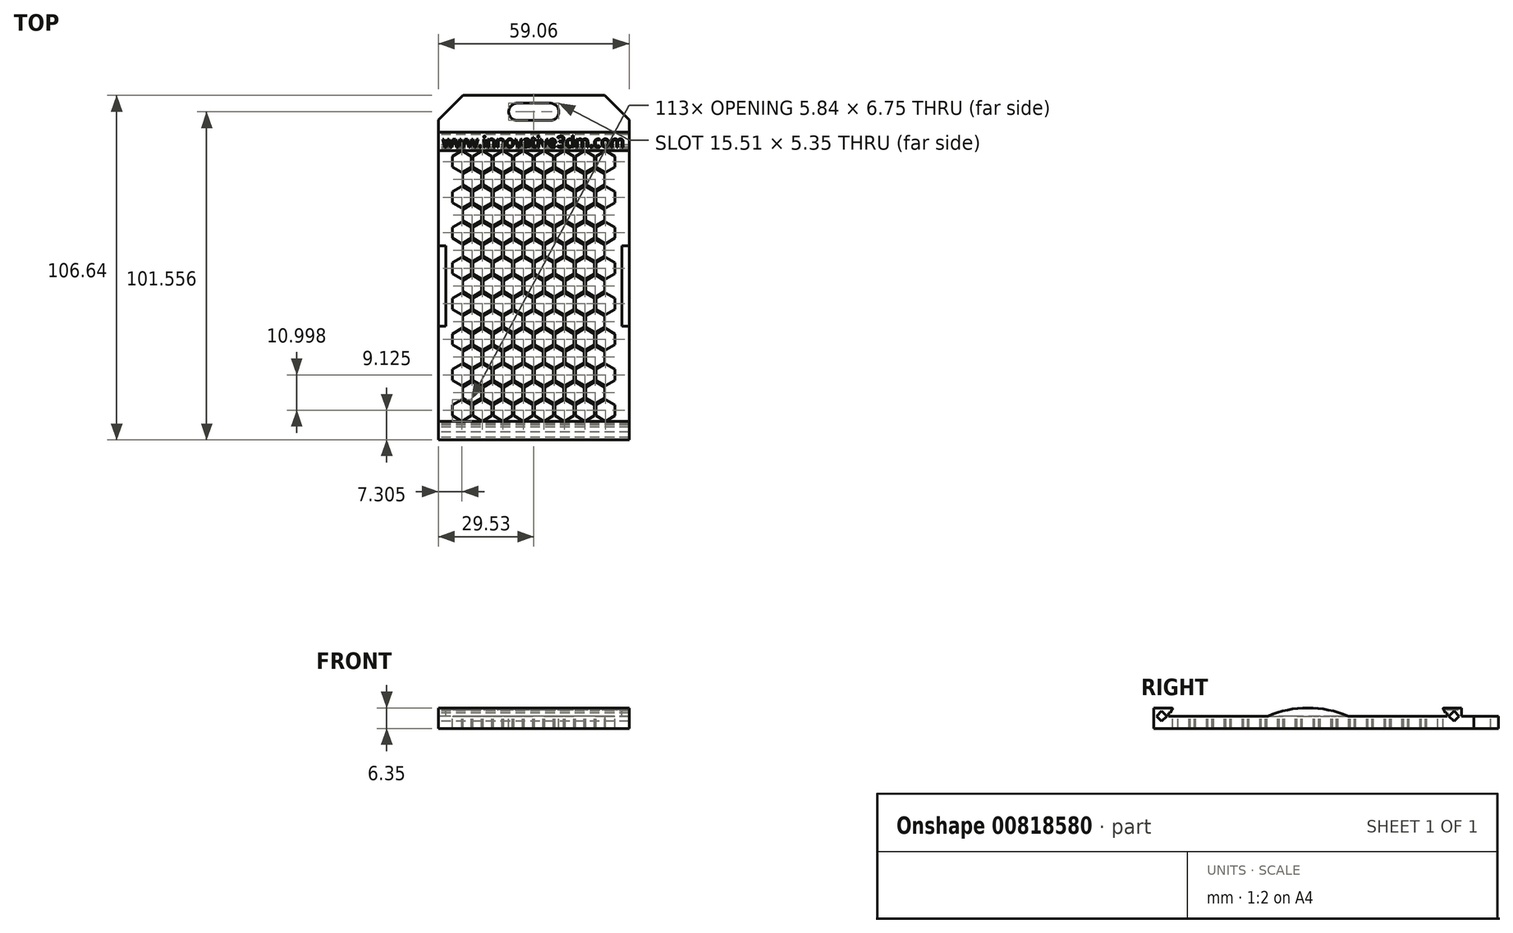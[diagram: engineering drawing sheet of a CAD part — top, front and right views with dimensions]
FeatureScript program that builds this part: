
annotation { "Feature Type Name" : "Feature", "Feature Type Description" : "" }
export const myFeature = defineFeature(function(context is Context, id is Id, definition is map)
    precondition{}
    {
        {
            var Q0;
            Q0=qCreatedBy(makeId("Right.planeOp"),FACE);
            var sketch = newSketch(context, id + "F0", { "sketchPlane" : qUnion([Q0])});
            skLineSegment(sketch, "E0.bottom", {"start": v(0, 0) * mm, "end": v(47.63, 0) * mm});
            skLineSegment(sketch, "E0.top", {"start": v(42.13, 6.35) * mm, "end": v(47.63, 6.35) * mm});
            skLineSegment(sketch, "E0.right", {"start": v(47.63, 0) * mm, "end": v(47.63, 6.35) * mm});
            skLineSegment(sketch, "E1", {"start": v(42.86, 3.81) * mm, "end": v(0, 3.81) * mm});
            skLineSegment(sketch, "E2", {"start": v(0, 0) * mm, "end": v(0, 12.7) * mm, "construction": true});
            skLineSegment(sketch, "E3.MirrorCS", {"start": v(0, 0) * mm, "end": v(-47.63, 0) * mm});
            skLineSegment(sketch, "E4.MirrorCS", {"start": v(-42.13, 6.35) * mm, "end": v(-47.63, 6.35) * mm});
            skLineSegment(sketch, "E5.MirrorCS", {"start": v(-47.63, 0) * mm, "end": v(-47.63, 6.35) * mm});
            skLineSegment(sketch, "E6.MirrorCS", {"start": v(-42.86, 3.81) * mm, "end": v(0, 3.81) * mm});
            skLineSegment(sketch, "E7", {"start": v(42.86, 3.81) * mm, "end": v(47.63, 3.81) * mm, "construction": true});
            skCircle(sketch, "E8.cCircle", {"center": v(45.24, 3.81) * mm, "radius": 1.59 * mm, "construction": true});
            skPoint(sketch, "E8.cCircle.perimeterSnap0", {"position": v(45.24, 3.81) * mm});
            skLineSegment(sketch, "E8.0", {"start": v(45.24, 2.22) * mm, "end": v(43.66, 3.8) * mm});
            skPoint(sketch, "E8.0.startSnap0", {"position": v(45.24, 3.81) * mm});
            skLineSegment(sketch, "E8.1", {"start": v(43.66, 3.81) * mm, "end": v(45.24, 5.4) * mm});
            skLineSegment(sketch, "E8.2", {"start": v(45.24, 5.4) * mm, "end": v(46.83, 3.81) * mm});
            skLineSegment(sketch, "E8.3", {"start": v(46.83, 3.81) * mm, "end": v(45.24, 2.22) * mm});
            skLineSegment(sketch, "E9.MirrorCS", {"start": v(-46.83, 3.81) * mm, "end": v(-45.24, 2.22) * mm});
            skLineSegment(sketch, "E10.MirrorCS", {"start": v(-45.24, 5.4) * mm, "end": v(-46.83, 3.81) * mm});
            skLineSegment(sketch, "E11.MirrorCS", {"start": v(-45.24, 2.22) * mm, "end": v(-43.66, 3.8) * mm});
            skLineSegment(sketch, "E12.MirrorCS", {"start": v(-43.66, 3.81) * mm, "end": v(-45.24, 5.4) * mm});
            skLineSegment(sketch, "E13.bottom", {"start": v(47.63, 3.81) * mm, "end": v(59.02, 3.81) * mm});
            skLineSegment(sketch, "E13.top", {"start": v(47.63, 0) * mm, "end": v(59.02, 0) * mm});
            skLineSegment(sketch, "E13.left", {"start": v(47.63, 3.81) * mm, "end": v(47.63, 0) * mm});
            skLineSegment(sketch, "E13.right", {"start": v(59.02, 3.81) * mm, "end": v(59.02, 0) * mm});
            skLineSegment(sketch, "E14", {"start": v(42.86, 4.83) * mm, "end": v(43.11, 4.83) * mm});
            skLineSegment(sketch, "E15", {"start": v(43.11, 4.83) * mm, "end": v(43.11, 3.81) * mm});
            skLineSegment(sketch, "E16", {"start": v(43.11, 3.81) * mm, "end": v(42.86, 3.81) * mm});
            skLineSegment(sketch, "E17", {"start": v(-42.86, 4.83) * mm, "end": v(-43.1, 4.83) * mm});
            skLineSegment(sketch, "E18", {"start": v(-43.1, 4.83) * mm, "end": v(-43.1, 3.81) * mm});
            skLineSegment(sketch, "E19", {"start": v(-43.1, 3.81) * mm, "end": v(-42.86, 3.81) * mm});
            skPoint(sketch, "E20.orphan", {"position": v(-42.06, 6.35) * mm});
            skPoint(sketch, "E21.visualSharp", {"position": v(-41.58, 6.35) * mm});
            skArc(sketch, "E21.filletArc", {"start": v(-41.93, 5.93) * mm, "mid": v(-41.9, 6.2) * mm, "end": v(-42.13, 6.35) * mm});
            skPoint(sketch, "E22.orphan", {"position": v(42.06, 6.35) * mm});
            skPoint(sketch, "E23.visualSharp", {"position": v(41.58, 6.35) * mm});
            skArc(sketch, "E23.filletArc", {"start": v(42.13, 6.35) * mm, "mid": v(41.9, 6.2) * mm, "end": v(41.93, 5.93) * mm});
            skLineSegment(sketch, "E24", {"start": v(42.86, 4.83) * mm, "end": v(42.6, 4.83) * mm});
            skLineSegment(sketch, "E25", {"start": v(42.6, 4.83) * mm, "end": v(41.93, 5.93) * mm});
            skLineSegment(sketch, "E26", {"start": v(-42.86, 4.83) * mm, "end": v(-42.6, 4.83) * mm});
            skLineSegment(sketch, "E27", {"start": v(-42.6, 4.83) * mm, "end": v(-41.93, 5.93) * mm});
            skSolve(sketch);
        }
        {
            var Q0;
            Q0 = qSketchRegion(id + "F0", true);
            extrude(context, id + "F1", {"entities" : qUnion([Q0]), "endBound" : BoundingType.SYMMETRIC, "depth" : 59.05 * mm, "offsetDistance" : 25.4 * mm});
        }
        {
            var Q0;
            Q0=makeQuery(id+"F1.opExtrude","CAP_FACE",FACE,{"disambiguationData":[OSD([sQuery(id+"F0.wireOp",EDGE,"E0.bottom"),sQuery(id+"F0.wireOp",EDGE,"E0.top"),sQuery(id+"F0.wireOp",EDGE,"E0.right"),sQuery(id+"F0.wireOp",EDGE,"gyNRLkVu-gDWa-j0yL-LBTd-Hr4iBRcMcfl1"),sQuery(id+"F0.wireOp",EDGE,"E1"),sQuery(id+"F0.wireOp",EDGE,"KyRSDgAd-UBMl-goyb-JxHU-d5xV0LulEB9J"),sQuery(id+"F0.wireOp",EDGE,"0e1NTcIS-lz3a-VeYZ-tNHN-98BEs02OGzgN"),sQuery(id+"F0.wireOp",EDGE,"e9ce5134-ec22-4a58-8b23-488e075d9638.filletArc"),sQuery(id+"F0.wireOp",EDGE,"9cae3bd2-e31c-4099-b72a-596a19319f310.MirrorCS"),sQuery(id+"F0.wireOp",EDGE,"9cae3bd2-e31c-4099-b72a-596a19319f311.MirrorCS"),sQuery(id+"F0.wireOp",EDGE,"9cae3bd2-e31c-4099-b72a-596a19319f312.MirrorCS"),sQuery(id+"F0.wireOp",EDGE,"9cae3bd2-e31c-4099-b72a-596a19319f313.MirrorCS"),sQuery(id+"F0.wireOp",EDGE,"E3.MirrorCS"),sQuery(id+"F0.wireOp",EDGE,"E4.MirrorCS"),sQuery(id+"F0.wireOp",EDGE,"E5.MirrorCS"),sQuery(id+"F0.wireOp",EDGE,"E6.MirrorCS")])],"isStart":false});
            var sketch = newSketch(context, id + "F2", { "sketchPlane" : qUnion([Q0])});
            skLineSegment(sketch, "E28", {"start": v(0, 0) * mm, "end": v(0, -25.4) * mm, "construction": true});
            skArc(sketch, "E29", {"start": v(19.05, 0) * mm, "mid": v(0, 6.35) * mm, "end": v(-19.05, 0) * mm});
            skLineSegment(sketch, "E30", {"start": v(19.05, 0) * mm, "end": v(-19.05, 0) * mm});
            skSolve(sketch);
        }
        {
            var Q0;
            {var subQ0=sQuery(id+"F2.wireOp",EDGE,"E29");var subQ1=makeQuery(id+"F1.opExtrude","CAP_EDGE",EDGE,{"disambiguationData":[OSD([sQuery(id+"F0.wireOp",EDGE,"E1"),sQuery(id+"F0.wireOp",EDGE,"E6.MirrorCS")])],"isStart":false});var subQ2=makeQuery(id+"F2.imprint","INTERSECT",VERTEX,{"disambiguationData":[OD(0.0)],"derivedFrom":[subQ1,subQ0]});Q0=makeQuery(id+"F2.imprint","IMPRINT",FACE,{"disambiguationData":[TD([[makeQuery(id+"F2.imprint","IMPRINT",EDGE,{"disambiguationData":[TD([[subQ2,-1.0]])],"derivedFrom":subQ0}),1.0]])]});}
            var Q1;
            Q1=sQuery(id+"F2.wireOp",EDGE,"E29");
            extrude(context, id + "F3", {"entities" : qUnion([Q0]), "operationType" : NewBodyOperationType.ADD, "surfaceEntities" : qUnion([Q1]), "oppositeDirection" : true, "depth" : 2.3 * mm, "offsetDistance" : 25.4 * mm});
        }
        {
            var Q0;
            Q0=makeQuery(id+"F1.opExtrude","SWEPT_BODY",BODY,{"disambiguationData":[OSD([sQuery(id+"F0.wireOp",EDGE,"E0.bottom"),sQuery(id+"F0.wireOp",EDGE,"E0.top"),sQuery(id+"F0.wireOp",EDGE,"E0.right"),sQuery(id+"F0.wireOp",EDGE,"gyNRLkVu-gDWa-j0yL-LBTd-Hr4iBRcMcfl1"),sQuery(id+"F0.wireOp",EDGE,"E1"),sQuery(id+"F0.wireOp",EDGE,"KyRSDgAd-UBMl-goyb-JxHU-d5xV0LulEB9J"),sQuery(id+"F0.wireOp",EDGE,"0e1NTcIS-lz3a-VeYZ-tNHN-98BEs02OGzgN"),sQuery(id+"F0.wireOp",EDGE,"e9ce5134-ec22-4a58-8b23-488e075d9638.filletArc"),sQuery(id+"F0.wireOp",EDGE,"9cae3bd2-e31c-4099-b72a-596a19319f310.MirrorCS"),sQuery(id+"F0.wireOp",EDGE,"9cae3bd2-e31c-4099-b72a-596a19319f311.MirrorCS"),sQuery(id+"F0.wireOp",EDGE,"9cae3bd2-e31c-4099-b72a-596a19319f312.MirrorCS"),sQuery(id+"F0.wireOp",EDGE,"9cae3bd2-e31c-4099-b72a-596a19319f313.MirrorCS"),sQuery(id+"F0.wireOp",EDGE,"E3.MirrorCS"),sQuery(id+"F0.wireOp",EDGE,"E4.MirrorCS"),sQuery(id+"F0.wireOp",EDGE,"E5.MirrorCS"),sQuery(id+"F0.wireOp",EDGE,"E6.MirrorCS")])]});
            var Q1;
            Q1=qCreatedBy(makeId("Right.planeOp"),FACE);
            mirror(context, id + "F4", {"operationType" : NewBodyOperationType.ADD, "entities" : qUnion([Q0]), "mirrorPlane" : qUnion([Q1])});
        }
        {
            var Q0;
            Q0=makeQuery(id+"F1.opExtrude","SWEPT_FACE",FACE,{"disambiguationData":[OSD([sQuery(id+"F0.wireOp",EDGE,"E1"),sQuery(id+"F0.wireOp",EDGE,"E6.MirrorCS")])]});
            var sketch = newSketch(context, id + "F5", { "sketchPlane" : qUnion([Q0])});
            skCircle(sketch, "E31.cCircle", {"center": v(0, 0) * mm, "radius": 2.92 * mm, "construction": true});
            skLineSegment(sketch, "E31.0", {"start": v(2.92, 1.69) * mm, "end": v(2.92, -1.69) * mm});
            skLineSegment(sketch, "E31.1", {"start": v(2.92, -1.69) * mm, "end": v(0, -3.37) * mm});
            skLineSegment(sketch, "E31.2", {"start": v(0, -3.37) * mm, "end": v(-2.92, -1.69) * mm});
            skLineSegment(sketch, "E31.3", {"start": v(-2.92, -1.69) * mm, "end": v(-2.92, 1.69) * mm});
            skLineSegment(sketch, "E31.4", {"start": v(-2.92, 1.69) * mm, "end": v(0, 3.37) * mm});
            skLineSegment(sketch, "E31.5", {"start": v(0, 3.37) * mm, "end": v(2.92, 1.69) * mm});
            skPoint(sketch, "E31.0.midPoint", {"position": v(2.92, 0) * mm});
            skLineSegment(sketch, "E32.1.0.0", {"start": v(6.35, 3.37) * mm, "end": v(9.27, 1.69) * mm});
            skLineSegment(sketch, "E32.1.0.1", {"start": v(3.43, 1.69) * mm, "end": v(6.35, 3.37) * mm});
            skLineSegment(sketch, "E32.1.0.2", {"start": v(3.43, -1.69) * mm, "end": v(3.43, 1.69) * mm});
            skLineSegment(sketch, "E32.1.0.3", {"start": v(6.35, -3.37) * mm, "end": v(3.43, -1.69) * mm});
            skLineSegment(sketch, "E32.1.0.4", {"start": v(9.27, -1.69) * mm, "end": v(6.35, -3.37) * mm});
            skLineSegment(sketch, "E32.1.0.5", {"start": v(9.27, 1.69) * mm, "end": v(9.27, -1.69) * mm});
            skLineSegment(sketch, "E32.2.0.0", {"start": v(12.7, 3.37) * mm, "end": v(15.62, 1.69) * mm});
            skLineSegment(sketch, "E32.2.0.1", {"start": v(9.78, 1.69) * mm, "end": v(12.7, 3.37) * mm});
            skLineSegment(sketch, "E32.2.0.2", {"start": v(9.78, -1.69) * mm, "end": v(9.78, 1.69) * mm});
            skLineSegment(sketch, "E32.2.0.3", {"start": v(12.7, -3.37) * mm, "end": v(9.78, -1.69) * mm});
            skLineSegment(sketch, "E32.2.0.4", {"start": v(15.62, -1.69) * mm, "end": v(12.7, -3.37) * mm});
            skLineSegment(sketch, "E32.2.0.5", {"start": v(15.62, 1.69) * mm, "end": v(15.62, -1.69) * mm});
            skLineSegment(sketch, "E32.direction1", {"start": v(-2.92, -1.69) * mm, "end": v(3.43, -1.69) * mm, "construction": true});
            skLineSegment(sketch, "E33.0.3.0", {"start": v(19.05, 3.37) * mm, "end": v(21.97, 1.69) * mm});
            skLineSegment(sketch, "E33.3.3.0", {"start": v(16.13, 1.69) * mm, "end": v(19.05, 3.37) * mm});
            skLineSegment(sketch, "E33.6.3.0", {"start": v(16.13, -1.69) * mm, "end": v(16.13, 1.69) * mm});
            skLineSegment(sketch, "E33.9.3.0", {"start": v(19.05, -3.37) * mm, "end": v(16.13, -1.69) * mm});
            skLineSegment(sketch, "E33.12.3.0", {"start": v(21.97, -1.69) * mm, "end": v(19.05, -3.37) * mm});
            skLineSegment(sketch, "E33.15.3.0", {"start": v(21.97, 1.69) * mm, "end": v(21.97, -1.69) * mm});
            skLineSegment(sketch, "E34", {"start": v(2.92, 1.69) * mm, "end": v(3.43, 1.69) * mm, "construction": true});
            skLineSegment(sketch, "E35", {"start": v(3.18, 1.69) * mm, "end": v(3.18, 5.5) * mm, "construction": true});
            skLineSegment(sketch, "E36.0", {"start": v(0.25, 3.81) * mm, "end": v(3.17, 2.13) * mm, "construction": true});
            skLineSegment(sketch, "E37", {"start": v(0, 0) * mm, "end": v(1.46, 2.53) * mm, "construction": true});
            skLineSegment(sketch, "E38", {"start": v(1.46, 2.53) * mm, "end": v(3.18, 5.5) * mm, "construction": true});
            skCircle(sketch, "E39.cCircle", {"center": v(3.18, 5.5) * mm, "radius": 2.92 * mm, "construction": true});
            skPoint(sketch, "E39.cCircle.perimeterSnap0", {"position": v(1.71, 2.97) * mm});
            skLineSegment(sketch, "E39.0", {"start": v(3.18, 2.13) * mm, "end": v(0.25, 3.81) * mm});
            skLineSegment(sketch, "E39.1", {"start": v(0.25, 3.81) * mm, "end": v(0.25, 7.19) * mm});
            skLineSegment(sketch, "E39.2", {"start": v(0.25, 7.19) * mm, "end": v(3.18, 8.87) * mm});
            skLineSegment(sketch, "E39.3", {"start": v(3.18, 8.87) * mm, "end": v(6.1, 7.19) * mm});
            skLineSegment(sketch, "E39.4", {"start": v(6.1, 7.19) * mm, "end": v(6.1, 3.81) * mm});
            skLineSegment(sketch, "E39.5", {"start": v(6.1, 3.81) * mm, "end": v(3.18, 2.13) * mm});
            skPoint(sketch, "E39.0.midPoint", {"position": v(1.71, 2.97) * mm});
            skPoint(sketch, "E39.0.midPoint.positionSnap0", {"position": v(1.71, 2.97) * mm});
            skLineSegment(sketch, "E40.1.0.0", {"start": v(6.6, 7.19) * mm, "end": v(9.53, 8.87) * mm});
            skLineSegment(sketch, "E40.1.0.1", {"start": v(9.52, 8.87) * mm, "end": v(12.45, 7.19) * mm});
            skLineSegment(sketch, "E40.1.0.2", {"start": v(12.45, 7.19) * mm, "end": v(12.45, 3.81) * mm});
            skLineSegment(sketch, "E40.1.0.3", {"start": v(12.45, 3.81) * mm, "end": v(9.52, 2.13) * mm});
            skLineSegment(sketch, "E40.1.0.4", {"start": v(9.52, 2.13) * mm, "end": v(6.6, 3.81) * mm});
            skLineSegment(sketch, "E40.1.0.5", {"start": v(6.6, 3.81) * mm, "end": v(6.6, 7.19) * mm});
            skLineSegment(sketch, "E40.2.0.0", {"start": v(12.95, 7.19) * mm, "end": v(15.88, 8.87) * mm});
            skLineSegment(sketch, "E40.2.0.1", {"start": v(15.87, 8.87) * mm, "end": v(18.8, 7.19) * mm});
            skLineSegment(sketch, "E40.2.0.2", {"start": v(18.8, 7.19) * mm, "end": v(18.8, 3.81) * mm});
            skLineSegment(sketch, "E40.2.0.3", {"start": v(18.8, 3.81) * mm, "end": v(15.87, 2.13) * mm});
            skLineSegment(sketch, "E40.2.0.4", {"start": v(15.88, 2.13) * mm, "end": v(12.95, 3.81) * mm});
            skLineSegment(sketch, "E40.2.0.5", {"start": v(12.95, 3.81) * mm, "end": v(12.95, 7.19) * mm});
            skLineSegment(sketch, "E40.direction1", {"start": v(0.25, 3.81) * mm, "end": v(6.6, 3.81) * mm, "construction": true});
            skLineSegment(sketch, "E41.0.3.0", {"start": v(19.3, 7.19) * mm, "end": v(22.23, 8.87) * mm});
            skLineSegment(sketch, "E41.3.3.0", {"start": v(22.23, 8.87) * mm, "end": v(25.15, 7.19) * mm});
            skLineSegment(sketch, "E41.6.3.0", {"start": v(25.15, 7.19) * mm, "end": v(25.15, 3.81) * mm});
            skLineSegment(sketch, "E41.9.3.0", {"start": v(25.15, 3.81) * mm, "end": v(22.23, 2.13) * mm});
            skLineSegment(sketch, "E41.12.3.0", {"start": v(22.23, 2.13) * mm, "end": v(19.3, 3.81) * mm});
            skLineSegment(sketch, "E41.15.3.0", {"start": v(19.3, 3.81) * mm, "end": v(19.3, 7.19) * mm});
            skLineSegment(sketch, "E42.1.0.0", {"start": v(-9.27, -1.69) * mm, "end": v(-9.27, 1.69) * mm});
            skLineSegment(sketch, "E42.1.0.1", {"start": v(-9.27, 1.69) * mm, "end": v(-6.35, 3.37) * mm});
            skLineSegment(sketch, "E42.1.0.2", {"start": v(-6.35, 3.37) * mm, "end": v(-3.43, 1.69) * mm});
            skLineSegment(sketch, "E42.1.0.3", {"start": v(-3.43, 1.69) * mm, "end": v(-3.43, -1.69) * mm});
            skLineSegment(sketch, "E42.1.0.4", {"start": v(-3.43, -1.69) * mm, "end": v(-6.35, -3.37) * mm});
            skLineSegment(sketch, "E42.1.0.5", {"start": v(-6.35, -3.37) * mm, "end": v(-9.27, -1.69) * mm});
            skLineSegment(sketch, "E42.2.0.0", {"start": v(-15.62, -1.69) * mm, "end": v(-15.62, 1.69) * mm});
            skLineSegment(sketch, "E42.2.0.1", {"start": v(-15.62, 1.69) * mm, "end": v(-12.7, 3.37) * mm});
            skLineSegment(sketch, "E42.2.0.2", {"start": v(-12.7, 3.37) * mm, "end": v(-9.78, 1.69) * mm});
            skLineSegment(sketch, "E42.2.0.3", {"start": v(-9.78, 1.69) * mm, "end": v(-9.78, -1.69) * mm});
            skLineSegment(sketch, "E42.2.0.4", {"start": v(-9.78, -1.69) * mm, "end": v(-12.7, -3.37) * mm});
            skLineSegment(sketch, "E42.2.0.5", {"start": v(-12.7, -3.37) * mm, "end": v(-15.62, -1.69) * mm});
            skLineSegment(sketch, "E42.direction1", {"start": v(-2.92, -1.69) * mm, "end": v(-9.27, -1.69) * mm, "construction": true});
            skLineSegment(sketch, "E43.0.3.0", {"start": v(-21.97, -1.69) * mm, "end": v(-21.97, 1.69) * mm});
            skLineSegment(sketch, "E43.3.3.0", {"start": v(-21.97, 1.69) * mm, "end": v(-19.05, 3.37) * mm});
            skLineSegment(sketch, "E43.6.3.0", {"start": v(-19.05, 3.37) * mm, "end": v(-16.13, 1.69) * mm});
            skLineSegment(sketch, "E43.9.3.0", {"start": v(-16.13, 1.69) * mm, "end": v(-16.13, -1.69) * mm});
            skLineSegment(sketch, "E43.12.3.0", {"start": v(-16.13, -1.69) * mm, "end": v(-19.05, -3.37) * mm});
            skLineSegment(sketch, "E43.15.3.0", {"start": v(-19.05, -3.37) * mm, "end": v(-21.97, -1.69) * mm});
            skLineSegment(sketch, "E44.1.0.0", {"start": v(-6.1, 3.81) * mm, "end": v(-6.1, 7.19) * mm});
            skLineSegment(sketch, "E44.1.0.1", {"start": v(-6.1, 7.19) * mm, "end": v(-3.17, 8.87) * mm});
            skLineSegment(sketch, "E44.1.0.2", {"start": v(-3.17, 8.87) * mm, "end": v(-0.25, 7.19) * mm});
            skLineSegment(sketch, "E44.1.0.3", {"start": v(-0.25, 3.81) * mm, "end": v(-3.18, 2.13) * mm});
            skLineSegment(sketch, "E44.1.0.4", {"start": v(-0.25, 7.19) * mm, "end": v(-0.25, 3.81) * mm});
            skLineSegment(sketch, "E44.1.0.5", {"start": v(-3.17, 2.13) * mm, "end": v(-6.1, 3.81) * mm});
            skLineSegment(sketch, "E44.2.0.0", {"start": v(-12.45, 3.81) * mm, "end": v(-12.45, 7.19) * mm});
            skLineSegment(sketch, "E44.2.0.1", {"start": v(-12.45, 7.19) * mm, "end": v(-9.52, 8.87) * mm});
            skLineSegment(sketch, "E44.2.0.2", {"start": v(-9.52, 8.87) * mm, "end": v(-6.6, 7.19) * mm});
            skLineSegment(sketch, "E44.2.0.3", {"start": v(-6.6, 3.81) * mm, "end": v(-9.52, 2.13) * mm});
            skLineSegment(sketch, "E44.2.0.4", {"start": v(-6.6, 7.19) * mm, "end": v(-6.6, 3.81) * mm});
            skLineSegment(sketch, "E44.2.0.5", {"start": v(-9.52, 2.13) * mm, "end": v(-12.45, 3.81) * mm});
            skLineSegment(sketch, "E44.3.0.0", {"start": v(-18.8, 3.81) * mm, "end": v(-18.8, 7.19) * mm});
            skLineSegment(sketch, "E44.3.0.1", {"start": v(-18.8, 7.19) * mm, "end": v(-15.88, 8.87) * mm});
            skLineSegment(sketch, "E44.3.0.2", {"start": v(-15.87, 8.87) * mm, "end": v(-12.95, 7.19) * mm});
            skLineSegment(sketch, "E44.3.0.3", {"start": v(-12.95, 3.81) * mm, "end": v(-15.88, 2.13) * mm});
            skLineSegment(sketch, "E44.3.0.4", {"start": v(-12.95, 7.19) * mm, "end": v(-12.95, 3.81) * mm});
            skLineSegment(sketch, "E44.3.0.5", {"start": v(-15.88, 2.13) * mm, "end": v(-18.8, 3.81) * mm});
            skLineSegment(sketch, "E44.4.0.0", {"start": v(-25.15, 3.81) * mm, "end": v(-25.15, 7.19) * mm});
            skLineSegment(sketch, "E44.4.0.1", {"start": v(-25.15, 7.19) * mm, "end": v(-22.23, 8.87) * mm});
            skLineSegment(sketch, "E44.4.0.2", {"start": v(-22.22, 8.87) * mm, "end": v(-19.3, 7.19) * mm});
            skLineSegment(sketch, "E44.4.0.3", {"start": v(-19.3, 3.81) * mm, "end": v(-22.23, 2.13) * mm});
            skLineSegment(sketch, "E44.4.0.4", {"start": v(-19.3, 7.19) * mm, "end": v(-19.3, 3.81) * mm});
            skLineSegment(sketch, "E44.4.0.5", {"start": v(-22.23, 2.13) * mm, "end": v(-25.15, 3.81) * mm});
            skLineSegment(sketch, "E44.direction1", {"start": v(0.25, 3.81) * mm, "end": v(-6.1, 3.81) * mm, "construction": true});
            skLineSegment(sketch, "E45.0.1.0", {"start": v(-9.78, 12.68) * mm, "end": v(-9.78, 9.31) * mm});
            skLineSegment(sketch, "E45.0.1.1", {"start": v(-12.45, 14.81) * mm, "end": v(-12.45, 18.18) * mm});
            skLineSegment(sketch, "E45.0.1.2", {"start": v(-21.97, 12.68) * mm, "end": v(-19.05, 14.37) * mm});
            skLineSegment(sketch, "E45.0.1.3", {"start": v(19.05, 7.63) * mm, "end": v(16.13, 9.31) * mm});
            skLineSegment(sketch, "E45.0.1.4", {"start": v(9.27, 12.68) * mm, "end": v(9.27, 9.31) * mm});
            skLineSegment(sketch, "E45.0.1.5", {"start": v(12.7, 7.63) * mm, "end": v(9.78, 9.31) * mm});
            skLineSegment(sketch, "E45.0.1.6", {"start": v(6.6, 18.18) * mm, "end": v(9.53, 19.87) * mm});
            skLineSegment(sketch, "E45.0.1.7", {"start": v(-9.27, 9.31) * mm, "end": v(-9.27, 12.68) * mm});
            skLineSegment(sketch, "E45.0.1.8", {"start": v(-6.6, 14.81) * mm, "end": v(-9.52, 13.12) * mm});
            skLineSegment(sketch, "E45.0.1.9", {"start": v(1.46, 13.53) * mm, "end": v(3.18, 16.5) * mm, "construction": true});
            skLineSegment(sketch, "E45.0.1.10", {"start": v(-6.35, 7.63) * mm, "end": v(-9.27, 9.31) * mm});
            skLineSegment(sketch, "E45.0.1.11", {"start": v(-16.13, 12.68) * mm, "end": v(-16.13, 9.31) * mm});
            skLineSegment(sketch, "E45.0.1.12", {"start": v(-18.8, 18.18) * mm, "end": v(-15.88, 19.87) * mm});
            skLineSegment(sketch, "E45.0.1.13", {"start": v(-12.95, 18.18) * mm, "end": v(-12.95, 14.81) * mm});
            skLineSegment(sketch, "E45.0.1.14", {"start": v(22.23, 19.87) * mm, "end": v(25.15, 18.18) * mm});
            skLineSegment(sketch, "E45.0.1.15", {"start": v(6.6, 14.81) * mm, "end": v(6.6, 18.18) * mm});
            skLineSegment(sketch, "E45.0.1.16", {"start": v(21.97, 12.68) * mm, "end": v(21.97, 9.31) * mm});
            skLineSegment(sketch, "E45.0.1.17", {"start": v(12.45, 14.81) * mm, "end": v(9.52, 13.12) * mm});
            skLineSegment(sketch, "E45.0.1.18", {"start": v(-19.05, 14.37) * mm, "end": v(-16.13, 12.68) * mm});
            skLineSegment(sketch, "E45.0.1.19", {"start": v(-18.8, 14.81) * mm, "end": v(-18.8, 18.18) * mm});
            skLineSegment(sketch, "E45.0.1.20", {"start": v(9.27, 9.31) * mm, "end": v(6.35, 7.63) * mm});
            skLineSegment(sketch, "E45.0.1.21", {"start": v(6.35, 7.63) * mm, "end": v(3.43, 9.31) * mm});
            skLineSegment(sketch, "E45.0.1.22", {"start": v(3.43, 9.31) * mm, "end": v(3.43, 12.68) * mm});
            skLineSegment(sketch, "E45.0.1.23", {"start": v(3.43, 12.68) * mm, "end": v(6.35, 14.37) * mm});
            skLineSegment(sketch, "E45.0.1.24", {"start": v(6.35, 14.37) * mm, "end": v(9.27, 12.68) * mm});
            skLineSegment(sketch, "E45.0.1.25", {"start": v(0, 14.37) * mm, "end": v(2.92, 12.68) * mm});
            skLineSegment(sketch, "E45.0.1.26", {"start": v(-0.25, 14.81) * mm, "end": v(-3.17, 13.12) * mm});
            skLineSegment(sketch, "E45.0.1.27", {"start": v(-6.6, 18.18) * mm, "end": v(-6.6, 14.81) * mm});
            skLineSegment(sketch, "E45.0.1.28", {"start": v(-25.15, 18.18) * mm, "end": v(-22.23, 19.87) * mm});
            skLineSegment(sketch, "E45.0.1.29", {"start": v(-2.92, 12.68) * mm, "end": v(0, 14.37) * mm});
            skCircle(sketch, "E45.0.1.30", {"center": v(3.18, 16.5) * mm, "radius": 2.92 * mm, "construction": true});
            skLineSegment(sketch, "E45.0.1.31", {"start": v(18.8, 14.81) * mm, "end": v(15.87, 13.12) * mm});
            skLineSegment(sketch, "E45.0.1.32", {"start": v(25.15, 14.81) * mm, "end": v(22.23, 13.12) * mm});
            skLineSegment(sketch, "E45.0.1.33", {"start": v(-21.97, 9.31) * mm, "end": v(-21.97, 12.68) * mm});
            skLineSegment(sketch, "E45.0.1.34", {"start": v(0, 7.63) * mm, "end": v(-2.92, 9.31) * mm});
            skLineSegment(sketch, "E45.0.1.35", {"start": v(2.92, 9.31) * mm, "end": v(0, 7.63) * mm});
            skLineSegment(sketch, "E45.0.1.36", {"start": v(2.92, 12.68) * mm, "end": v(2.92, 9.31) * mm});
            skCircle(sketch, "E45.0.1.37", {"center": v(0, 11) * mm, "radius": 2.92 * mm, "construction": true});
            skLineSegment(sketch, "E45.0.1.38", {"start": v(9.78, 9.31) * mm, "end": v(9.78, 12.68) * mm});
            skLineSegment(sketch, "E45.0.1.39", {"start": v(9.78, 12.68) * mm, "end": v(12.7, 14.37) * mm});
            skLineSegment(sketch, "E45.0.1.40", {"start": v(12.7, 14.37) * mm, "end": v(15.62, 12.68) * mm});
            skLineSegment(sketch, "E45.0.1.41", {"start": v(21.97, 9.31) * mm, "end": v(19.05, 7.63) * mm});
            skLineSegment(sketch, "E45.0.1.42", {"start": v(12.45, 18.18) * mm, "end": v(12.45, 14.81) * mm});
            skLineSegment(sketch, "E45.0.1.43", {"start": v(-3.17, 19.87) * mm, "end": v(-0.25, 18.18) * mm});
            skLineSegment(sketch, "E45.0.1.44", {"start": v(6.1, 14.81) * mm, "end": v(3.18, 13.12) * mm});
            skLineSegment(sketch, "E45.0.1.45", {"start": v(16.13, 12.68) * mm, "end": v(19.05, 14.37) * mm});
            skLineSegment(sketch, "E45.0.1.46", {"start": v(18.8, 18.18) * mm, "end": v(18.8, 14.81) * mm});
            skLineSegment(sketch, "E45.0.1.47", {"start": v(25.15, 18.18) * mm, "end": v(25.15, 14.81) * mm});
            skLineSegment(sketch, "E45.0.1.48", {"start": v(-2.92, 9.31) * mm, "end": v(-9.27, 9.31) * mm, "construction": true});
            skLineSegment(sketch, "E45.0.1.49", {"start": v(-3.17, 13.12) * mm, "end": v(-6.1, 14.81) * mm});
            skLineSegment(sketch, "E45.0.1.50", {"start": v(-3.43, 12.68) * mm, "end": v(-3.43, 9.31) * mm});
            skLineSegment(sketch, "E45.0.1.51", {"start": v(-6.1, 14.81) * mm, "end": v(-6.1, 18.18) * mm});
            skLineSegment(sketch, "E45.0.1.52", {"start": v(0.25, 14.81) * mm, "end": v(3.17, 13.12) * mm, "construction": true});
            skLineSegment(sketch, "E45.0.1.53", {"start": v(15.62, 9.31) * mm, "end": v(12.7, 7.63) * mm});
            skLineSegment(sketch, "E45.0.1.54", {"start": v(12.95, 14.81) * mm, "end": v(12.95, 18.18) * mm});
            skLineSegment(sketch, "E45.0.1.55", {"start": v(22.23, 13.12) * mm, "end": v(19.3, 14.81) * mm});
            skLineSegment(sketch, "E45.0.1.56", {"start": v(-15.88, 13.12) * mm, "end": v(-18.8, 14.81) * mm});
            skLineSegment(sketch, "E45.0.1.57", {"start": v(19.05, 14.37) * mm, "end": v(21.97, 12.68) * mm});
            skLineSegment(sketch, "E45.0.1.58", {"start": v(6.1, 18.18) * mm, "end": v(6.1, 14.81) * mm});
            skLineSegment(sketch, "E45.0.1.59", {"start": v(0, 11) * mm, "end": v(1.46, 13.53) * mm, "construction": true});
            skLineSegment(sketch, "E45.0.1.60", {"start": v(15.87, 19.87) * mm, "end": v(18.8, 18.18) * mm});
            skLineSegment(sketch, "E45.0.1.61", {"start": v(-9.52, 13.12) * mm, "end": v(-12.45, 14.81) * mm});
            skLineSegment(sketch, "E45.0.1.62", {"start": v(9.52, 19.87) * mm, "end": v(12.45, 18.18) * mm});
            skLineSegment(sketch, "E45.0.1.63", {"start": v(-6.35, 14.37) * mm, "end": v(-3.43, 12.68) * mm});
            skLineSegment(sketch, "E45.0.1.64", {"start": v(-12.95, 14.81) * mm, "end": v(-15.88, 13.12) * mm});
            skLineSegment(sketch, "E45.0.1.65", {"start": v(3.18, 12.68) * mm, "end": v(3.18, 16.5) * mm, "construction": true});
            skLineSegment(sketch, "E45.0.1.66", {"start": v(-15.62, 12.68) * mm, "end": v(-12.7, 14.37) * mm});
            skPoint(sketch, "E45.0.1.67", {"position": v(2.92, 11) * mm});
            skLineSegment(sketch, "E45.0.1.68", {"start": v(-9.78, 9.31) * mm, "end": v(-12.7, 7.63) * mm});
            skLineSegment(sketch, "E45.0.1.69", {"start": v(-0.25, 18.18) * mm, "end": v(-0.25, 14.81) * mm});
            skLineSegment(sketch, "E45.0.1.70", {"start": v(-15.87, 19.87) * mm, "end": v(-12.95, 18.18) * mm});
            skLineSegment(sketch, "E45.0.1.71", {"start": v(15.62, 12.68) * mm, "end": v(15.62, 9.31) * mm});
            skLineSegment(sketch, "E45.0.1.72", {"start": v(-22.22, 19.87) * mm, "end": v(-19.3, 18.18) * mm});
            skLineSegment(sketch, "E45.0.1.73", {"start": v(-19.3, 18.18) * mm, "end": v(-19.3, 14.81) * mm});
            skLineSegment(sketch, "E45.0.1.74", {"start": v(19.3, 14.81) * mm, "end": v(19.3, 18.18) * mm});
            skLineSegment(sketch, "E45.0.1.75", {"start": v(-19.3, 14.81) * mm, "end": v(-22.23, 13.12) * mm});
            skLineSegment(sketch, "E45.0.1.76", {"start": v(0.25, 14.81) * mm, "end": v(0.25, 18.18) * mm});
            skLineSegment(sketch, "E45.0.1.77", {"start": v(-12.7, 14.37) * mm, "end": v(-9.78, 12.68) * mm});
            skLineSegment(sketch, "E45.0.1.78", {"start": v(15.88, 13.12) * mm, "end": v(12.95, 14.81) * mm});
            skLineSegment(sketch, "E45.0.1.79", {"start": v(16.13, 9.31) * mm, "end": v(16.13, 12.68) * mm});
            skLineSegment(sketch, "E45.0.1.80", {"start": v(-15.62, 9.31) * mm, "end": v(-15.62, 12.68) * mm});
            skLineSegment(sketch, "E45.0.1.81", {"start": v(-2.92, 9.31) * mm, "end": v(-2.92, 12.68) * mm});
            skLineSegment(sketch, "E45.0.1.82", {"start": v(12.95, 18.18) * mm, "end": v(15.88, 19.87) * mm});
            skPoint(sketch, "E45.0.1.83", {"position": v(1.71, 13.97) * mm});
            skLineSegment(sketch, "E45.0.1.84", {"start": v(-9.52, 19.87) * mm, "end": v(-6.6, 18.18) * mm});
            skLineSegment(sketch, "E45.0.1.85", {"start": v(-6.1, 18.18) * mm, "end": v(-3.17, 19.87) * mm});
            skLineSegment(sketch, "E45.0.1.86", {"start": v(0.25, 14.81) * mm, "end": v(-6.1, 14.81) * mm, "construction": true});
            skLineSegment(sketch, "E45.0.1.87", {"start": v(-3.43, 9.31) * mm, "end": v(-6.35, 7.63) * mm});
            skLineSegment(sketch, "E45.0.1.88", {"start": v(-22.23, 13.12) * mm, "end": v(-25.15, 14.81) * mm});
            skLineSegment(sketch, "E45.0.1.89", {"start": v(-12.45, 18.18) * mm, "end": v(-9.52, 19.87) * mm});
            skLineSegment(sketch, "E45.0.1.90", {"start": v(-2.92, 9.31) * mm, "end": v(3.43, 9.31) * mm, "construction": true});
            skLineSegment(sketch, "E45.0.1.91", {"start": v(3.18, 19.87) * mm, "end": v(6.1, 18.18) * mm});
            skLineSegment(sketch, "E45.0.1.92", {"start": v(19.3, 18.18) * mm, "end": v(22.23, 19.87) * mm});
            skLineSegment(sketch, "E45.0.1.93", {"start": v(-9.27, 12.68) * mm, "end": v(-6.35, 14.37) * mm});
            skLineSegment(sketch, "E45.0.1.94", {"start": v(9.52, 13.12) * mm, "end": v(6.6, 14.81) * mm});
            skLineSegment(sketch, "E45.0.1.95", {"start": v(0.25, 18.18) * mm, "end": v(3.18, 19.87) * mm});
            skLineSegment(sketch, "E45.0.1.96", {"start": v(0.25, 14.81) * mm, "end": v(6.6, 14.81) * mm, "construction": true});
            skLineSegment(sketch, "E45.0.1.97", {"start": v(3.18, 13.12) * mm, "end": v(0.25, 14.81) * mm});
            skPoint(sketch, "E45.0.1.98", {"position": v(1.71, 13.97) * mm});
            skPoint(sketch, "E45.0.1.99", {"position": v(1.71, 13.97) * mm});
            skLineSegment(sketch, "E45.0.1.100", {"start": v(2.92, 12.68) * mm, "end": v(3.43, 12.68) * mm, "construction": true});
            skLineSegment(sketch, "E45.0.1.101", {"start": v(-25.15, 14.81) * mm, "end": v(-25.15, 18.18) * mm});
            skLineSegment(sketch, "E45.0.1.102", {"start": v(-19.05, 7.63) * mm, "end": v(-21.97, 9.31) * mm});
            skLineSegment(sketch, "E45.0.1.103", {"start": v(-16.13, 9.31) * mm, "end": v(-19.05, 7.63) * mm});
            skLineSegment(sketch, "E45.0.1.104", {"start": v(-12.7, 7.63) * mm, "end": v(-15.62, 9.31) * mm});
            skLineSegment(sketch, "E45.0.2.0", {"start": v(-9.78, 23.68) * mm, "end": v(-9.78, 20.31) * mm});
            skLineSegment(sketch, "E45.0.2.1", {"start": v(-12.45, 25.8) * mm, "end": v(-12.45, 29.18) * mm});
            skLineSegment(sketch, "E45.0.2.2", {"start": v(-21.97, 23.68) * mm, "end": v(-19.05, 25.37) * mm});
            skLineSegment(sketch, "E45.0.2.3", {"start": v(19.05, 18.62) * mm, "end": v(16.13, 20.31) * mm});
            skLineSegment(sketch, "E45.0.2.4", {"start": v(9.27, 23.68) * mm, "end": v(9.27, 20.31) * mm});
            skLineSegment(sketch, "E45.0.2.5", {"start": v(12.7, 18.62) * mm, "end": v(9.78, 20.31) * mm});
            skLineSegment(sketch, "E45.0.2.6", {"start": v(6.6, 29.18) * mm, "end": v(9.53, 30.87) * mm});
            skLineSegment(sketch, "E45.0.2.7", {"start": v(-9.27, 20.31) * mm, "end": v(-9.27, 23.68) * mm});
            skLineSegment(sketch, "E45.0.2.8", {"start": v(-6.6, 25.8) * mm, "end": v(-9.52, 24.12) * mm});
            skLineSegment(sketch, "E45.0.2.9", {"start": v(1.46, 24.53) * mm, "end": v(3.18, 27.5) * mm, "construction": true});
            skLineSegment(sketch, "E45.0.2.10", {"start": v(-6.35, 18.62) * mm, "end": v(-9.27, 20.31) * mm});
            skLineSegment(sketch, "E45.0.2.11", {"start": v(-16.13, 23.68) * mm, "end": v(-16.13, 20.31) * mm});
            skLineSegment(sketch, "E45.0.2.12", {"start": v(-18.8, 29.18) * mm, "end": v(-15.88, 30.87) * mm});
            skLineSegment(sketch, "E45.0.2.13", {"start": v(-12.95, 29.18) * mm, "end": v(-12.95, 25.8) * mm});
            skLineSegment(sketch, "E45.0.2.14", {"start": v(22.23, 30.87) * mm, "end": v(25.15, 29.18) * mm});
            skLineSegment(sketch, "E45.0.2.15", {"start": v(6.6, 25.8) * mm, "end": v(6.6, 29.18) * mm});
            skLineSegment(sketch, "E45.0.2.16", {"start": v(21.97, 23.68) * mm, "end": v(21.97, 20.31) * mm});
            skLineSegment(sketch, "E45.0.2.17", {"start": v(12.45, 25.8) * mm, "end": v(9.52, 24.12) * mm});
            skLineSegment(sketch, "E45.0.2.18", {"start": v(-19.05, 25.37) * mm, "end": v(-16.13, 23.68) * mm});
            skLineSegment(sketch, "E45.0.2.19", {"start": v(-18.8, 25.8) * mm, "end": v(-18.8, 29.18) * mm});
            skLineSegment(sketch, "E45.0.2.20", {"start": v(9.27, 20.31) * mm, "end": v(6.35, 18.62) * mm});
            skLineSegment(sketch, "E45.0.2.21", {"start": v(6.35, 18.62) * mm, "end": v(3.43, 20.31) * mm});
            skLineSegment(sketch, "E45.0.2.22", {"start": v(3.43, 20.31) * mm, "end": v(3.43, 23.68) * mm});
            skLineSegment(sketch, "E45.0.2.23", {"start": v(3.43, 23.68) * mm, "end": v(6.35, 25.37) * mm});
            skLineSegment(sketch, "E45.0.2.24", {"start": v(6.35, 25.37) * mm, "end": v(9.27, 23.68) * mm});
            skLineSegment(sketch, "E45.0.2.25", {"start": v(0, 25.37) * mm, "end": v(2.92, 23.68) * mm});
            skLineSegment(sketch, "E45.0.2.26", {"start": v(-0.25, 25.8) * mm, "end": v(-3.17, 24.12) * mm});
            skLineSegment(sketch, "E45.0.2.27", {"start": v(-6.6, 29.18) * mm, "end": v(-6.6, 25.8) * mm});
            skLineSegment(sketch, "E45.0.2.28", {"start": v(-25.15, 29.18) * mm, "end": v(-22.23, 30.87) * mm});
            skLineSegment(sketch, "E45.0.2.29", {"start": v(-2.92, 23.68) * mm, "end": v(0, 25.37) * mm});
            skCircle(sketch, "E45.0.2.30", {"center": v(3.18, 27.5) * mm, "radius": 2.92 * mm, "construction": true});
            skLineSegment(sketch, "E45.0.2.31", {"start": v(18.8, 25.8) * mm, "end": v(15.87, 24.12) * mm});
            skLineSegment(sketch, "E45.0.2.32", {"start": v(25.15, 25.8) * mm, "end": v(22.23, 24.12) * mm});
            skLineSegment(sketch, "E45.0.2.33", {"start": v(-21.97, 20.31) * mm, "end": v(-21.97, 23.68) * mm});
            skLineSegment(sketch, "E45.0.2.34", {"start": v(0, 18.62) * mm, "end": v(-2.92, 20.31) * mm});
            skLineSegment(sketch, "E45.0.2.35", {"start": v(2.92, 20.31) * mm, "end": v(0, 18.62) * mm});
            skLineSegment(sketch, "E45.0.2.36", {"start": v(2.92, 23.68) * mm, "end": v(2.92, 20.31) * mm});
            skCircle(sketch, "E45.0.2.37", {"center": v(0, 22) * mm, "radius": 2.92 * mm, "construction": true});
            skLineSegment(sketch, "E45.0.2.38", {"start": v(9.78, 20.31) * mm, "end": v(9.78, 23.68) * mm});
            skLineSegment(sketch, "E45.0.2.39", {"start": v(9.78, 23.68) * mm, "end": v(12.7, 25.37) * mm});
            skLineSegment(sketch, "E45.0.2.40", {"start": v(12.7, 25.37) * mm, "end": v(15.62, 23.68) * mm});
            skLineSegment(sketch, "E45.0.2.41", {"start": v(21.97, 20.31) * mm, "end": v(19.05, 18.62) * mm});
            skLineSegment(sketch, "E45.0.2.42", {"start": v(12.45, 29.18) * mm, "end": v(12.45, 25.8) * mm});
            skLineSegment(sketch, "E45.0.2.43", {"start": v(-3.17, 30.87) * mm, "end": v(-0.25, 29.18) * mm});
            skLineSegment(sketch, "E45.0.2.44", {"start": v(6.1, 25.8) * mm, "end": v(3.17, 24.12) * mm});
            skLineSegment(sketch, "E45.0.2.45", {"start": v(16.13, 23.68) * mm, "end": v(19.05, 25.37) * mm});
            skLineSegment(sketch, "E45.0.2.46", {"start": v(18.8, 29.18) * mm, "end": v(18.8, 25.8) * mm});
            skLineSegment(sketch, "E45.0.2.47", {"start": v(25.15, 29.18) * mm, "end": v(25.15, 25.8) * mm});
            skLineSegment(sketch, "E45.0.2.48", {"start": v(-2.92, 20.31) * mm, "end": v(-9.27, 20.31) * mm, "construction": true});
            skLineSegment(sketch, "E45.0.2.49", {"start": v(-3.17, 24.12) * mm, "end": v(-6.1, 25.8) * mm});
            skLineSegment(sketch, "E45.0.2.50", {"start": v(-3.43, 23.68) * mm, "end": v(-3.43, 20.31) * mm});
            skLineSegment(sketch, "E45.0.2.51", {"start": v(-6.1, 25.8) * mm, "end": v(-6.1, 29.18) * mm});
            skLineSegment(sketch, "E45.0.2.52", {"start": v(0.25, 25.8) * mm, "end": v(3.17, 24.12) * mm, "construction": true});
            skLineSegment(sketch, "E45.0.2.53", {"start": v(15.62, 20.31) * mm, "end": v(12.7, 18.62) * mm});
            skLineSegment(sketch, "E45.0.2.54", {"start": v(12.95, 25.8) * mm, "end": v(12.95, 29.18) * mm});
            skLineSegment(sketch, "E45.0.2.55", {"start": v(22.23, 24.12) * mm, "end": v(19.3, 25.8) * mm});
            skLineSegment(sketch, "E45.0.2.56", {"start": v(-15.88, 24.12) * mm, "end": v(-18.8, 25.8) * mm});
            skLineSegment(sketch, "E45.0.2.57", {"start": v(19.05, 25.37) * mm, "end": v(21.97, 23.68) * mm});
            skLineSegment(sketch, "E45.0.2.58", {"start": v(6.1, 29.18) * mm, "end": v(6.1, 25.8) * mm});
            skLineSegment(sketch, "E45.0.2.59", {"start": v(0, 22) * mm, "end": v(1.46, 24.53) * mm, "construction": true});
            skLineSegment(sketch, "E45.0.2.60", {"start": v(15.87, 30.87) * mm, "end": v(18.8, 29.18) * mm});
            skLineSegment(sketch, "E45.0.2.61", {"start": v(-9.52, 24.12) * mm, "end": v(-12.45, 25.8) * mm});
            skLineSegment(sketch, "E45.0.2.62", {"start": v(9.52, 30.87) * mm, "end": v(12.45, 29.18) * mm});
            skLineSegment(sketch, "E45.0.2.63", {"start": v(-6.35, 25.37) * mm, "end": v(-3.43, 23.68) * mm});
            skLineSegment(sketch, "E45.0.2.64", {"start": v(-12.95, 25.8) * mm, "end": v(-15.88, 24.12) * mm});
            skLineSegment(sketch, "E45.0.2.65", {"start": v(3.18, 23.68) * mm, "end": v(3.18, 27.5) * mm, "construction": true});
            skLineSegment(sketch, "E45.0.2.66", {"start": v(-15.62, 23.68) * mm, "end": v(-12.7, 25.37) * mm});
            skPoint(sketch, "E45.0.2.67", {"position": v(2.92, 22) * mm});
            skLineSegment(sketch, "E45.0.2.68", {"start": v(-9.78, 20.31) * mm, "end": v(-12.7, 18.62) * mm});
            skLineSegment(sketch, "E45.0.2.69", {"start": v(-0.25, 29.18) * mm, "end": v(-0.25, 25.8) * mm});
            skLineSegment(sketch, "E45.0.2.70", {"start": v(-15.87, 30.87) * mm, "end": v(-12.95, 29.18) * mm});
            skLineSegment(sketch, "E45.0.2.71", {"start": v(15.62, 23.68) * mm, "end": v(15.62, 20.31) * mm});
            skLineSegment(sketch, "E45.0.2.72", {"start": v(-22.22, 30.87) * mm, "end": v(-19.3, 29.18) * mm});
            skLineSegment(sketch, "E45.0.2.73", {"start": v(-19.3, 29.18) * mm, "end": v(-19.3, 25.8) * mm});
            skLineSegment(sketch, "E45.0.2.74", {"start": v(19.3, 25.8) * mm, "end": v(19.3, 29.18) * mm});
            skLineSegment(sketch, "E45.0.2.75", {"start": v(-19.3, 25.8) * mm, "end": v(-22.23, 24.12) * mm});
            skLineSegment(sketch, "E45.0.2.76", {"start": v(0.25, 25.8) * mm, "end": v(0.25, 29.18) * mm});
            skLineSegment(sketch, "E45.0.2.77", {"start": v(-12.7, 25.37) * mm, "end": v(-9.78, 23.68) * mm});
            skLineSegment(sketch, "E45.0.2.78", {"start": v(15.88, 24.12) * mm, "end": v(12.95, 25.8) * mm});
            skLineSegment(sketch, "E45.0.2.79", {"start": v(16.13, 20.31) * mm, "end": v(16.13, 23.68) * mm});
            skLineSegment(sketch, "E45.0.2.80", {"start": v(-15.62, 20.31) * mm, "end": v(-15.62, 23.68) * mm});
            skLineSegment(sketch, "E45.0.2.81", {"start": v(-2.92, 20.31) * mm, "end": v(-2.92, 23.68) * mm});
            skLineSegment(sketch, "E45.0.2.82", {"start": v(12.95, 29.18) * mm, "end": v(15.88, 30.87) * mm});
            skPoint(sketch, "E45.0.2.83", {"position": v(1.71, 24.97) * mm});
            skLineSegment(sketch, "E45.0.2.84", {"start": v(-9.52, 30.87) * mm, "end": v(-6.6, 29.18) * mm});
            skLineSegment(sketch, "E45.0.2.85", {"start": v(-6.1, 29.18) * mm, "end": v(-3.17, 30.87) * mm});
            skLineSegment(sketch, "E45.0.2.86", {"start": v(0.25, 25.8) * mm, "end": v(-6.1, 25.8) * mm, "construction": true});
            skLineSegment(sketch, "E45.0.2.87", {"start": v(-3.43, 20.31) * mm, "end": v(-6.35, 18.62) * mm});
            skLineSegment(sketch, "E45.0.2.88", {"start": v(-22.23, 24.12) * mm, "end": v(-25.15, 25.8) * mm});
            skLineSegment(sketch, "E45.0.2.89", {"start": v(-12.45, 29.18) * mm, "end": v(-9.52, 30.87) * mm});
            skLineSegment(sketch, "E45.0.2.90", {"start": v(-2.92, 20.31) * mm, "end": v(3.43, 20.31) * mm, "construction": true});
            skLineSegment(sketch, "E45.0.2.91", {"start": v(3.18, 30.87) * mm, "end": v(6.1, 29.18) * mm});
            skLineSegment(sketch, "E45.0.2.92", {"start": v(19.3, 29.18) * mm, "end": v(22.23, 30.87) * mm});
            skLineSegment(sketch, "E45.0.2.93", {"start": v(-9.27, 23.68) * mm, "end": v(-6.35, 25.37) * mm});
            skLineSegment(sketch, "E45.0.2.94", {"start": v(9.52, 24.12) * mm, "end": v(6.6, 25.8) * mm});
            skLineSegment(sketch, "E45.0.2.95", {"start": v(0.25, 29.18) * mm, "end": v(3.18, 30.87) * mm});
            skLineSegment(sketch, "E45.0.2.96", {"start": v(0.25, 25.8) * mm, "end": v(6.6, 25.8) * mm, "construction": true});
            skLineSegment(sketch, "E45.0.2.97", {"start": v(3.18, 24.12) * mm, "end": v(0.25, 25.8) * mm});
            skPoint(sketch, "E45.0.2.98", {"position": v(1.71, 24.97) * mm});
            skPoint(sketch, "E45.0.2.99", {"position": v(1.71, 24.97) * mm});
            skLineSegment(sketch, "E45.0.2.100", {"start": v(2.92, 23.68) * mm, "end": v(3.43, 23.68) * mm, "construction": true});
            skLineSegment(sketch, "E45.0.2.101", {"start": v(-25.15, 25.8) * mm, "end": v(-25.15, 29.18) * mm});
            skLineSegment(sketch, "E45.0.2.102", {"start": v(-19.05, 18.62) * mm, "end": v(-21.97, 20.31) * mm});
            skLineSegment(sketch, "E45.0.2.103", {"start": v(-16.13, 20.31) * mm, "end": v(-19.05, 18.62) * mm});
            skLineSegment(sketch, "E45.0.2.104", {"start": v(-12.7, 18.62) * mm, "end": v(-15.62, 20.31) * mm});
            skLineSegment(sketch, "E45.0.3.0", {"start": v(-9.78, 34.68) * mm, "end": v(-9.78, 31.3) * mm});
            skLineSegment(sketch, "E45.0.3.1", {"start": v(-12.45, 36.8) * mm, "end": v(-12.45, 40.18) * mm});
            skLineSegment(sketch, "E45.0.3.2", {"start": v(-21.97, 34.68) * mm, "end": v(-19.05, 36.37) * mm});
            skLineSegment(sketch, "E45.0.3.3", {"start": v(19.05, 29.62) * mm, "end": v(16.13, 31.3) * mm});
            skLineSegment(sketch, "E45.0.3.4", {"start": v(9.27, 34.68) * mm, "end": v(9.27, 31.3) * mm});
            skLineSegment(sketch, "E45.0.3.5", {"start": v(12.7, 29.62) * mm, "end": v(9.78, 31.3) * mm});
            skLineSegment(sketch, "E45.0.3.6", {"start": v(6.6, 40.18) * mm, "end": v(9.53, 41.87) * mm});
            skLineSegment(sketch, "E45.0.3.7", {"start": v(-9.27, 31.3) * mm, "end": v(-9.27, 34.68) * mm});
            skLineSegment(sketch, "E45.0.3.8", {"start": v(-6.6, 36.8) * mm, "end": v(-9.52, 35.12) * mm});
            skLineSegment(sketch, "E45.0.3.9", {"start": v(1.46, 35.53) * mm, "end": v(3.18, 38.5) * mm, "construction": true});
            skLineSegment(sketch, "E45.0.3.10", {"start": v(-6.35, 29.62) * mm, "end": v(-9.27, 31.3) * mm});
            skLineSegment(sketch, "E45.0.3.11", {"start": v(-16.13, 34.68) * mm, "end": v(-16.13, 31.3) * mm});
            skLineSegment(sketch, "E45.0.3.12", {"start": v(-18.8, 40.18) * mm, "end": v(-15.88, 41.87) * mm});
            skLineSegment(sketch, "E45.0.3.13", {"start": v(-12.95, 40.18) * mm, "end": v(-12.95, 36.8) * mm});
            skLineSegment(sketch, "E45.0.3.14", {"start": v(22.23, 41.87) * mm, "end": v(25.15, 40.18) * mm});
            skLineSegment(sketch, "E45.0.3.15", {"start": v(6.6, 36.8) * mm, "end": v(6.6, 40.18) * mm});
            skLineSegment(sketch, "E45.0.3.16", {"start": v(21.97, 34.68) * mm, "end": v(21.97, 31.3) * mm});
            skLineSegment(sketch, "E45.0.3.17", {"start": v(12.45, 36.8) * mm, "end": v(9.52, 35.12) * mm});
            skLineSegment(sketch, "E45.0.3.18", {"start": v(-19.05, 36.37) * mm, "end": v(-16.13, 34.68) * mm});
            skLineSegment(sketch, "E45.0.3.19", {"start": v(-18.8, 36.8) * mm, "end": v(-18.8, 40.18) * mm});
            skLineSegment(sketch, "E45.0.3.20", {"start": v(9.27, 31.3) * mm, "end": v(6.35, 29.62) * mm});
            skLineSegment(sketch, "E45.0.3.21", {"start": v(6.35, 29.62) * mm, "end": v(3.43, 31.3) * mm});
            skLineSegment(sketch, "E45.0.3.22", {"start": v(3.43, 31.3) * mm, "end": v(3.43, 34.68) * mm});
            skLineSegment(sketch, "E45.0.3.23", {"start": v(3.43, 34.68) * mm, "end": v(6.35, 36.37) * mm});
            skLineSegment(sketch, "E45.0.3.24", {"start": v(6.35, 36.37) * mm, "end": v(9.27, 34.68) * mm});
            skLineSegment(sketch, "E45.0.3.25", {"start": v(0, 36.37) * mm, "end": v(2.92, 34.68) * mm});
            skLineSegment(sketch, "E45.0.3.26", {"start": v(-0.25, 36.8) * mm, "end": v(-3.17, 35.12) * mm});
            skLineSegment(sketch, "E45.0.3.27", {"start": v(-6.6, 40.18) * mm, "end": v(-6.6, 36.8) * mm});
            skLineSegment(sketch, "E45.0.3.28", {"start": v(-25.15, 40.18) * mm, "end": v(-22.23, 41.87) * mm});
            skLineSegment(sketch, "E45.0.3.29", {"start": v(-2.92, 34.68) * mm, "end": v(0, 36.37) * mm});
            skCircle(sketch, "E45.0.3.30", {"center": v(3.18, 38.5) * mm, "radius": 2.92 * mm, "construction": true});
            skLineSegment(sketch, "E45.0.3.31", {"start": v(18.8, 36.8) * mm, "end": v(15.87, 35.12) * mm});
            skLineSegment(sketch, "E45.0.3.32", {"start": v(25.15, 36.8) * mm, "end": v(22.23, 35.12) * mm});
            skLineSegment(sketch, "E45.0.3.33", {"start": v(-21.97, 31.3) * mm, "end": v(-21.97, 34.68) * mm});
            skLineSegment(sketch, "E45.0.3.34", {"start": v(0, 29.62) * mm, "end": v(-2.92, 31.3) * mm});
            skLineSegment(sketch, "E45.0.3.35", {"start": v(2.92, 31.3) * mm, "end": v(0, 29.62) * mm});
            skLineSegment(sketch, "E45.0.3.36", {"start": v(2.92, 34.68) * mm, "end": v(2.92, 31.3) * mm});
            skCircle(sketch, "E45.0.3.37", {"center": v(0, 33) * mm, "radius": 2.92 * mm, "construction": true});
            skLineSegment(sketch, "E45.0.3.38", {"start": v(9.78, 31.3) * mm, "end": v(9.78, 34.68) * mm});
            skLineSegment(sketch, "E45.0.3.39", {"start": v(9.78, 34.68) * mm, "end": v(12.7, 36.37) * mm});
            skLineSegment(sketch, "E45.0.3.40", {"start": v(12.7, 36.37) * mm, "end": v(15.62, 34.68) * mm});
            skLineSegment(sketch, "E45.0.3.41", {"start": v(21.97, 31.3) * mm, "end": v(19.05, 29.62) * mm});
            skLineSegment(sketch, "E45.0.3.42", {"start": v(12.45, 40.18) * mm, "end": v(12.45, 36.8) * mm});
            skLineSegment(sketch, "E45.0.3.43", {"start": v(-3.17, 41.87) * mm, "end": v(-0.25, 40.18) * mm});
            skLineSegment(sketch, "E45.0.3.44", {"start": v(6.1, 36.8) * mm, "end": v(3.18, 35.12) * mm});
            skLineSegment(sketch, "E45.0.3.45", {"start": v(16.13, 34.68) * mm, "end": v(19.05, 36.37) * mm});
            skLineSegment(sketch, "E45.0.3.46", {"start": v(18.8, 40.18) * mm, "end": v(18.8, 36.8) * mm});
            skLineSegment(sketch, "E45.0.3.47", {"start": v(25.15, 40.18) * mm, "end": v(25.15, 36.8) * mm});
            skLineSegment(sketch, "E45.0.3.48", {"start": v(-2.92, 31.3) * mm, "end": v(-9.27, 31.3) * mm, "construction": true});
            skLineSegment(sketch, "E45.0.3.49", {"start": v(-3.17, 35.12) * mm, "end": v(-6.1, 36.8) * mm});
            skLineSegment(sketch, "E45.0.3.50", {"start": v(-3.43, 34.68) * mm, "end": v(-3.43, 31.3) * mm});
            skLineSegment(sketch, "E45.0.3.51", {"start": v(-6.1, 36.8) * mm, "end": v(-6.1, 40.18) * mm});
            skLineSegment(sketch, "E45.0.3.52", {"start": v(0.25, 36.8) * mm, "end": v(3.17, 35.12) * mm, "construction": true});
            skLineSegment(sketch, "E45.0.3.53", {"start": v(15.62, 31.3) * mm, "end": v(12.7, 29.62) * mm});
            skLineSegment(sketch, "E45.0.3.54", {"start": v(12.95, 36.8) * mm, "end": v(12.95, 40.18) * mm});
            skLineSegment(sketch, "E45.0.3.55", {"start": v(22.23, 35.12) * mm, "end": v(19.3, 36.8) * mm});
            skLineSegment(sketch, "E45.0.3.56", {"start": v(-15.88, 35.12) * mm, "end": v(-18.8, 36.8) * mm});
            skLineSegment(sketch, "E45.0.3.57", {"start": v(19.05, 36.37) * mm, "end": v(21.97, 34.68) * mm});
            skLineSegment(sketch, "E45.0.3.58", {"start": v(6.1, 40.18) * mm, "end": v(6.1, 36.8) * mm});
            skLineSegment(sketch, "E45.0.3.59", {"start": v(0, 33) * mm, "end": v(1.46, 35.53) * mm, "construction": true});
            skLineSegment(sketch, "E45.0.3.60", {"start": v(15.87, 41.87) * mm, "end": v(18.8, 40.18) * mm});
            skLineSegment(sketch, "E45.0.3.61", {"start": v(-9.52, 35.12) * mm, "end": v(-12.45, 36.8) * mm});
            skLineSegment(sketch, "E45.0.3.62", {"start": v(9.52, 41.87) * mm, "end": v(12.45, 40.18) * mm});
            skLineSegment(sketch, "E45.0.3.63", {"start": v(-6.35, 36.37) * mm, "end": v(-3.43, 34.68) * mm});
            skLineSegment(sketch, "E45.0.3.64", {"start": v(-12.95, 36.8) * mm, "end": v(-15.88, 35.12) * mm});
            skLineSegment(sketch, "E45.0.3.65", {"start": v(3.18, 34.68) * mm, "end": v(3.18, 38.5) * mm, "construction": true});
            skLineSegment(sketch, "E45.0.3.66", {"start": v(-15.62, 34.68) * mm, "end": v(-12.7, 36.37) * mm});
            skPoint(sketch, "E45.0.3.67", {"position": v(2.92, 33) * mm});
            skLineSegment(sketch, "E45.0.3.68", {"start": v(-9.78, 31.3) * mm, "end": v(-12.7, 29.62) * mm});
            skLineSegment(sketch, "E45.0.3.69", {"start": v(-0.25, 40.18) * mm, "end": v(-0.25, 36.8) * mm});
            skLineSegment(sketch, "E45.0.3.70", {"start": v(-15.87, 41.87) * mm, "end": v(-12.95, 40.18) * mm});
            skLineSegment(sketch, "E45.0.3.71", {"start": v(15.62, 34.68) * mm, "end": v(15.62, 31.3) * mm});
            skLineSegment(sketch, "E45.0.3.72", {"start": v(-22.22, 41.87) * mm, "end": v(-19.3, 40.18) * mm});
            skLineSegment(sketch, "E45.0.3.73", {"start": v(-19.3, 40.18) * mm, "end": v(-19.3, 36.8) * mm});
            skLineSegment(sketch, "E45.0.3.74", {"start": v(19.3, 36.8) * mm, "end": v(19.3, 40.18) * mm});
            skLineSegment(sketch, "E45.0.3.75", {"start": v(-19.3, 36.8) * mm, "end": v(-22.23, 35.12) * mm});
            skLineSegment(sketch, "E45.0.3.76", {"start": v(0.25, 36.8) * mm, "end": v(0.25, 40.18) * mm});
            skLineSegment(sketch, "E45.0.3.77", {"start": v(-12.7, 36.37) * mm, "end": v(-9.78, 34.68) * mm});
            skLineSegment(sketch, "E45.0.3.78", {"start": v(15.88, 35.12) * mm, "end": v(12.95, 36.8) * mm});
            skLineSegment(sketch, "E45.0.3.79", {"start": v(16.13, 31.3) * mm, "end": v(16.13, 34.68) * mm});
            skLineSegment(sketch, "E45.0.3.80", {"start": v(-15.62, 31.3) * mm, "end": v(-15.62, 34.68) * mm});
            skLineSegment(sketch, "E45.0.3.81", {"start": v(-2.92, 31.3) * mm, "end": v(-2.92, 34.68) * mm});
            skLineSegment(sketch, "E45.0.3.82", {"start": v(12.95, 40.18) * mm, "end": v(15.88, 41.87) * mm});
            skPoint(sketch, "E45.0.3.83", {"position": v(1.71, 35.97) * mm});
            skLineSegment(sketch, "E45.0.3.84", {"start": v(-9.52, 41.87) * mm, "end": v(-6.6, 40.18) * mm});
            skLineSegment(sketch, "E45.0.3.85", {"start": v(-6.1, 40.18) * mm, "end": v(-3.17, 41.87) * mm});
            skLineSegment(sketch, "E45.0.3.86", {"start": v(0.25, 36.8) * mm, "end": v(-6.1, 36.8) * mm, "construction": true});
            skLineSegment(sketch, "E45.0.3.87", {"start": v(-3.43, 31.3) * mm, "end": v(-6.35, 29.62) * mm});
            skLineSegment(sketch, "E45.0.3.88", {"start": v(-22.23, 35.12) * mm, "end": v(-25.15, 36.8) * mm});
            skLineSegment(sketch, "E45.0.3.89", {"start": v(-12.45, 40.18) * mm, "end": v(-9.52, 41.87) * mm});
            skLineSegment(sketch, "E45.0.3.90", {"start": v(-2.92, 31.3) * mm, "end": v(3.43, 31.3) * mm, "construction": true});
            skLineSegment(sketch, "E45.0.3.91", {"start": v(3.18, 41.87) * mm, "end": v(6.1, 40.18) * mm});
            skLineSegment(sketch, "E45.0.3.92", {"start": v(19.3, 40.18) * mm, "end": v(22.23, 41.87) * mm});
            skLineSegment(sketch, "E45.0.3.93", {"start": v(-9.27, 34.68) * mm, "end": v(-6.35, 36.37) * mm});
            skLineSegment(sketch, "E45.0.3.94", {"start": v(9.52, 35.12) * mm, "end": v(6.6, 36.8) * mm});
            skLineSegment(sketch, "E45.0.3.95", {"start": v(0.25, 40.18) * mm, "end": v(3.18, 41.87) * mm});
            skLineSegment(sketch, "E45.0.3.96", {"start": v(0.25, 36.8) * mm, "end": v(6.6, 36.8) * mm, "construction": true});
            skLineSegment(sketch, "E45.0.3.97", {"start": v(3.18, 35.12) * mm, "end": v(0.25, 36.8) * mm});
            skPoint(sketch, "E45.0.3.98", {"position": v(1.71, 35.97) * mm});
            skPoint(sketch, "E45.0.3.99", {"position": v(1.71, 35.97) * mm});
            skLineSegment(sketch, "E45.0.3.100", {"start": v(2.92, 34.68) * mm, "end": v(3.43, 34.68) * mm, "construction": true});
            skLineSegment(sketch, "E45.0.3.101", {"start": v(-25.15, 36.8) * mm, "end": v(-25.15, 40.18) * mm});
            skLineSegment(sketch, "E45.0.3.102", {"start": v(-19.05, 29.62) * mm, "end": v(-21.97, 31.3) * mm});
            skLineSegment(sketch, "E45.0.3.103", {"start": v(-16.13, 31.3) * mm, "end": v(-19.05, 29.62) * mm});
            skLineSegment(sketch, "E45.0.3.104", {"start": v(-12.7, 29.62) * mm, "end": v(-15.62, 31.3) * mm});
            skLineSegment(sketch, "E45.direction1", {"start": v(-21.97, -1.69) * mm, "end": v(3.43, -1.69) * mm, "construction": true});
            skLineSegment(sketch, "E45.direction2", {"start": v(-21.97, -1.69) * mm, "end": v(-21.97, 9.31) * mm, "construction": true});
            skLineSegment(sketch, "E46.0.1.0", {"start": v(-0.25, -7.19) * mm, "end": v(-3.17, -8.87) * mm});
            skLineSegment(sketch, "E46.0.1.1", {"start": v(18.8, -3.81) * mm, "end": v(18.8, -7.19) * mm});
            skLineSegment(sketch, "E46.0.1.2", {"start": v(-15.88, -8.87) * mm, "end": v(-18.8, -7.19) * mm});
            skLineSegment(sketch, "E46.0.1.3", {"start": v(-19.3, -3.81) * mm, "end": v(-19.3, -7.19) * mm});
            skLineSegment(sketch, "E46.0.1.4", {"start": v(-3.17, -8.87) * mm, "end": v(-6.1, -7.19) * mm});
            skLineSegment(sketch, "E46.0.1.5", {"start": v(12.95, -7.19) * mm, "end": v(12.95, -3.81) * mm});
            skLineSegment(sketch, "E46.0.1.6", {"start": v(-3.43, -12.68) * mm, "end": v(-6.35, -14.37) * mm});
            skLineSegment(sketch, "E46.0.1.7", {"start": v(-15.62, -9.31) * mm, "end": v(-12.7, -7.63) * mm});
            skLineSegment(sketch, "E46.0.1.8", {"start": v(12.7, -14.37) * mm, "end": v(9.78, -12.68) * mm});
            skLineSegment(sketch, "E46.0.1.9", {"start": v(15.62, -12.68) * mm, "end": v(12.7, -14.37) * mm});
            skPoint(sketch, "E46.0.1.10", {"position": v(2.92, -11) * mm});
            skPoint(sketch, "E46.0.1.11", {"position": v(1.71, -8.03) * mm});
            skCircle(sketch, "E46.0.1.12", {"center": v(3.18, -5.5) * mm, "radius": 2.92 * mm, "construction": true});
            skLineSegment(sketch, "E46.0.1.13", {"start": v(18.8, -7.19) * mm, "end": v(15.87, -8.87) * mm});
            skLineSegment(sketch, "E46.0.1.14", {"start": v(15.88, -8.87) * mm, "end": v(12.95, -7.19) * mm});
            skLineSegment(sketch, "E46.0.1.15", {"start": v(-12.45, -7.19) * mm, "end": v(-12.45, -3.81) * mm});
            skLineSegment(sketch, "E46.0.1.16", {"start": v(-0.25, -3.81) * mm, "end": v(-0.25, -7.19) * mm});
            skLineSegment(sketch, "E46.0.1.17", {"start": v(-12.7, -7.63) * mm, "end": v(-9.78, -9.31) * mm});
            skLineSegment(sketch, "E46.0.1.18", {"start": v(-15.62, -12.68) * mm, "end": v(-15.62, -9.31) * mm});
            skLineSegment(sketch, "E46.0.1.19", {"start": v(-19.3, -7.19) * mm, "end": v(-22.23, -8.87) * mm});
            skLineSegment(sketch, "E46.0.1.20", {"start": v(0.25, -7.19) * mm, "end": v(0.25, -3.81) * mm});
            skLineSegment(sketch, "E46.0.1.21", {"start": v(-9.78, -9.31) * mm, "end": v(-9.78, -12.68) * mm});
            skLineSegment(sketch, "E46.0.1.22", {"start": v(15.62, -9.31) * mm, "end": v(15.62, -12.68) * mm});
            skLineSegment(sketch, "E46.0.1.23", {"start": v(-9.78, -12.68) * mm, "end": v(-12.7, -14.37) * mm});
            skLineSegment(sketch, "E46.0.1.24", {"start": v(-22.23, -8.87) * mm, "end": v(-25.15, -7.19) * mm});
            skLineSegment(sketch, "E46.0.1.25", {"start": v(-21.97, -12.68) * mm, "end": v(3.43, -12.68) * mm, "construction": true});
            skLineSegment(sketch, "E46.0.1.26", {"start": v(-12.7, -14.37) * mm, "end": v(-15.62, -12.68) * mm});
            skLineSegment(sketch, "E46.0.1.27", {"start": v(19.05, -7.63) * mm, "end": v(21.97, -9.31) * mm});
            skLineSegment(sketch, "E46.0.1.28", {"start": v(0.25, -7.19) * mm, "end": v(-6.1, -7.19) * mm, "construction": true});
            skLineSegment(sketch, "E46.0.1.29", {"start": v(-21.97, -12.68) * mm, "end": v(-21.97, -1.69) * mm, "construction": true});
            skLineSegment(sketch, "E46.0.1.30", {"start": v(-2.92, -12.68) * mm, "end": v(-9.27, -12.68) * mm, "construction": true});
            skLineSegment(sketch, "E46.0.1.31", {"start": v(25.15, -3.81) * mm, "end": v(25.15, -7.19) * mm});
            skLineSegment(sketch, "E46.0.1.32", {"start": v(16.13, -9.31) * mm, "end": v(19.05, -7.63) * mm});
            skLineSegment(sketch, "E46.0.1.33", {"start": v(-6.6, -7.19) * mm, "end": v(-9.52, -8.87) * mm});
            skLineSegment(sketch, "E46.0.1.34", {"start": v(25.15, -7.19) * mm, "end": v(22.23, -8.87) * mm});
            skLineSegment(sketch, "E46.0.1.35", {"start": v(16.13, -12.68) * mm, "end": v(16.13, -9.31) * mm});
            skLineSegment(sketch, "E46.0.1.36", {"start": v(-6.6, -3.81) * mm, "end": v(-6.6, -7.19) * mm});
            skLineSegment(sketch, "E46.0.1.37", {"start": v(19.05, -14.37) * mm, "end": v(16.13, -12.68) * mm});
            skLineSegment(sketch, "E46.0.1.38", {"start": v(-9.52, -8.87) * mm, "end": v(-12.45, -7.19) * mm});
            skLineSegment(sketch, "E46.0.1.39", {"start": v(-21.97, -9.31) * mm, "end": v(-19.05, -7.63) * mm});
            skLineSegment(sketch, "E46.0.1.40", {"start": v(22.23, -8.87) * mm, "end": v(19.3, -7.19) * mm});
            skLineSegment(sketch, "E46.0.1.41", {"start": v(12.45, -3.81) * mm, "end": v(12.45, -7.19) * mm});
            skLineSegment(sketch, "E46.0.1.42", {"start": v(21.97, -12.68) * mm, "end": v(19.05, -14.37) * mm});
            skLineSegment(sketch, "E46.0.1.43", {"start": v(-18.8, -7.19) * mm, "end": v(-18.8, -3.81) * mm});
            skLineSegment(sketch, "E46.0.1.44", {"start": v(-19.05, -7.63) * mm, "end": v(-16.13, -9.31) * mm});
            skLineSegment(sketch, "E46.0.1.45", {"start": v(19.3, -7.19) * mm, "end": v(19.3, -3.81) * mm});
            skLineSegment(sketch, "E46.0.1.46", {"start": v(12.45, -7.19) * mm, "end": v(9.52, -8.87) * mm});
            skLineSegment(sketch, "E46.0.1.47", {"start": v(21.97, -9.31) * mm, "end": v(21.97, -12.68) * mm});
            skLineSegment(sketch, "E46.0.1.48", {"start": v(-16.13, -9.31) * mm, "end": v(-16.13, -12.68) * mm});
            skLineSegment(sketch, "E46.0.1.49", {"start": v(-9.27, -12.68) * mm, "end": v(-9.27, -9.31) * mm});
            skLineSegment(sketch, "E46.0.1.50", {"start": v(-16.13, -12.68) * mm, "end": v(-19.05, -14.37) * mm});
            skLineSegment(sketch, "E46.0.1.51", {"start": v(-9.27, -9.31) * mm, "end": v(-6.35, -7.63) * mm});
            skLineSegment(sketch, "E46.0.1.52", {"start": v(6.6, -7.19) * mm, "end": v(6.6, -3.81) * mm});
            skLineSegment(sketch, "E46.0.1.53", {"start": v(-12.95, -7.19) * mm, "end": v(-15.88, -8.87) * mm});
            skLineSegment(sketch, "E46.0.1.54", {"start": v(-19.05, -14.37) * mm, "end": v(-21.97, -12.68) * mm});
            skLineSegment(sketch, "E46.0.1.55", {"start": v(-6.35, -7.63) * mm, "end": v(-3.43, -9.31) * mm});
            skLineSegment(sketch, "E46.0.1.56", {"start": v(-12.95, -3.81) * mm, "end": v(-12.95, -7.19) * mm});
            skLineSegment(sketch, "E46.0.1.57", {"start": v(-6.1, -7.19) * mm, "end": v(-6.1, -3.81) * mm});
            skLineSegment(sketch, "E46.0.1.58", {"start": v(-3.43, -9.31) * mm, "end": v(-3.43, -12.68) * mm});
            skLineSegment(sketch, "E46.0.1.59", {"start": v(12.7, -7.63) * mm, "end": v(15.62, -9.31) * mm});
            skLineSegment(sketch, "E46.0.1.60", {"start": v(9.78, -9.31) * mm, "end": v(12.7, -7.63) * mm});
            skLineSegment(sketch, "E46.0.1.61", {"start": v(9.78, -12.68) * mm, "end": v(9.78, -9.31) * mm});
            skCircle(sketch, "E46.0.1.62", {"center": v(0, -11) * mm, "radius": 2.92 * mm, "construction": true});
            skLineSegment(sketch, "E46.0.1.63", {"start": v(6.35, -14.37) * mm, "end": v(3.43, -12.68) * mm});
            skLineSegment(sketch, "E46.0.1.64", {"start": v(9.27, -12.68) * mm, "end": v(6.35, -14.37) * mm});
            skLineSegment(sketch, "E46.0.1.65", {"start": v(9.27, -9.31) * mm, "end": v(9.27, -12.68) * mm});
            skPoint(sketch, "E46.0.1.66", {"position": v(1.71, -8.03) * mm});
            skLineSegment(sketch, "E46.0.1.67", {"start": v(-6.35, -14.37) * mm, "end": v(-9.27, -12.68) * mm});
            skLineSegment(sketch, "E46.0.1.68", {"start": v(0, -11) * mm, "end": v(1.46, -8.47) * mm, "construction": true});
            skLineSegment(sketch, "E46.0.1.69", {"start": v(0.25, -7.19) * mm, "end": v(6.6, -7.19) * mm, "construction": true});
            skLineSegment(sketch, "E46.0.1.70", {"start": v(-2.92, -12.68) * mm, "end": v(3.43, -12.68) * mm, "construction": true});
            skLineSegment(sketch, "E46.0.1.71", {"start": v(6.1, -3.81) * mm, "end": v(6.1, -7.19) * mm});
            skLineSegment(sketch, "E46.0.1.72", {"start": v(6.1, -7.19) * mm, "end": v(3.18, -8.87) * mm});
            skLineSegment(sketch, "E46.0.1.73", {"start": v(-21.97, -12.68) * mm, "end": v(-21.97, -9.31) * mm});
            skLineSegment(sketch, "E46.0.1.74", {"start": v(9.52, -8.87) * mm, "end": v(6.6, -7.19) * mm});
            skLineSegment(sketch, "E46.0.1.75", {"start": v(3.18, -9.31) * mm, "end": v(3.18, -5.5) * mm, "construction": true});
            skLineSegment(sketch, "E46.0.1.76", {"start": v(2.92, -9.31) * mm, "end": v(2.92, -12.68) * mm});
            skLineSegment(sketch, "E46.0.1.77", {"start": v(2.92, -12.68) * mm, "end": v(0, -14.37) * mm});
            skLineSegment(sketch, "E46.0.1.78", {"start": v(0, -14.37) * mm, "end": v(-2.92, -12.68) * mm});
            skLineSegment(sketch, "E46.0.1.79", {"start": v(-2.92, -12.68) * mm, "end": v(-2.92, -9.31) * mm});
            skLineSegment(sketch, "E46.0.1.80", {"start": v(-2.92, -9.31) * mm, "end": v(0, -7.63) * mm});
            skLineSegment(sketch, "E46.0.1.81", {"start": v(6.35, -7.63) * mm, "end": v(9.27, -9.31) * mm});
            skLineSegment(sketch, "E46.0.1.82", {"start": v(3.43, -9.31) * mm, "end": v(6.35, -7.63) * mm});
            skLineSegment(sketch, "E46.0.1.83", {"start": v(3.43, -12.68) * mm, "end": v(3.43, -9.31) * mm});
            skPoint(sketch, "E46.0.1.84", {"position": v(1.71, -8.03) * mm});
            skLineSegment(sketch, "E46.0.1.85", {"start": v(22.23, -2.13) * mm, "end": v(25.15, -3.81) * mm});
            skLineSegment(sketch, "E46.0.1.86", {"start": v(9.52, -2.13) * mm, "end": v(12.45, -3.81) * mm});
            skLineSegment(sketch, "E46.0.1.87", {"start": v(1.46, -8.47) * mm, "end": v(3.18, -5.5) * mm, "construction": true});
            skLineSegment(sketch, "E46.0.1.88", {"start": v(-6.1, -3.81) * mm, "end": v(-3.17, -2.13) * mm});
            skLineSegment(sketch, "E46.0.1.89", {"start": v(-3.17, -2.13) * mm, "end": v(-0.25, -3.81) * mm});
            skLineSegment(sketch, "E46.0.1.90", {"start": v(15.87, -2.13) * mm, "end": v(18.8, -3.81) * mm});
            skLineSegment(sketch, "E46.0.1.91", {"start": v(-22.22, -2.13) * mm, "end": v(-19.3, -3.81) * mm});
            skLineSegment(sketch, "E46.0.1.92", {"start": v(0.25, -3.81) * mm, "end": v(3.18, -2.13) * mm});
            skLineSegment(sketch, "E46.0.1.93", {"start": v(19.3, -3.81) * mm, "end": v(22.23, -2.13) * mm});
            skLineSegment(sketch, "E46.0.1.94", {"start": v(3.18, -2.13) * mm, "end": v(6.1, -3.81) * mm});
            skLineSegment(sketch, "E46.0.1.95", {"start": v(-12.45, -3.81) * mm, "end": v(-9.52, -2.13) * mm});
            skLineSegment(sketch, "E46.0.1.96", {"start": v(-9.52, -2.13) * mm, "end": v(-6.6, -3.81) * mm});
            skLineSegment(sketch, "E46.0.1.97", {"start": v(6.6, -3.81) * mm, "end": v(9.53, -2.13) * mm});
            skLineSegment(sketch, "E46.0.1.98", {"start": v(-18.8, -3.81) * mm, "end": v(-15.88, -2.13) * mm});
            skLineSegment(sketch, "E46.0.1.99", {"start": v(2.92, -9.31) * mm, "end": v(3.43, -9.31) * mm, "construction": true});
            skLineSegment(sketch, "E46.0.1.100", {"start": v(-15.87, -2.13) * mm, "end": v(-12.95, -3.81) * mm});
            skLineSegment(sketch, "E46.0.1.101", {"start": v(12.95, -3.81) * mm, "end": v(15.88, -2.13) * mm});
            skLineSegment(sketch, "E46.0.1.102", {"start": v(0.25, -7.19) * mm, "end": v(3.17, -8.87) * mm, "construction": true});
            skLineSegment(sketch, "E46.0.1.103", {"start": v(0, -7.63) * mm, "end": v(2.92, -9.31) * mm});
            skLineSegment(sketch, "E46.0.1.104", {"start": v(3.18, -8.87) * mm, "end": v(0.25, -7.19) * mm});
            skLineSegment(sketch, "E46.0.1.105", {"start": v(-25.15, -7.19) * mm, "end": v(-25.15, -3.81) * mm});
            skLineSegment(sketch, "E46.0.1.106", {"start": v(-25.15, -3.81) * mm, "end": v(-22.23, -2.13) * mm});
            skLineSegment(sketch, "E46.0.2.0", {"start": v(-0.25, -18.18) * mm, "end": v(-3.17, -19.87) * mm});
            skLineSegment(sketch, "E46.0.2.1", {"start": v(18.8, -14.81) * mm, "end": v(18.8, -18.18) * mm});
            skLineSegment(sketch, "E46.0.2.2", {"start": v(-15.88, -19.87) * mm, "end": v(-18.8, -18.18) * mm});
            skLineSegment(sketch, "E46.0.2.3", {"start": v(-19.3, -14.81) * mm, "end": v(-19.3, -18.18) * mm});
            skLineSegment(sketch, "E46.0.2.4", {"start": v(-3.17, -19.87) * mm, "end": v(-6.1, -18.18) * mm});
            skLineSegment(sketch, "E46.0.2.5", {"start": v(12.95, -18.18) * mm, "end": v(12.95, -14.81) * mm});
            skLineSegment(sketch, "E46.0.2.6", {"start": v(-3.43, -23.68) * mm, "end": v(-6.35, -25.37) * mm});
            skLineSegment(sketch, "E46.0.2.7", {"start": v(-15.62, -20.31) * mm, "end": v(-12.7, -18.62) * mm});
            skLineSegment(sketch, "E46.0.2.8", {"start": v(12.7, -25.37) * mm, "end": v(9.78, -23.68) * mm});
            skLineSegment(sketch, "E46.0.2.9", {"start": v(15.62, -23.68) * mm, "end": v(12.7, -25.37) * mm});
            skPoint(sketch, "E46.0.2.10", {"position": v(2.92, -22) * mm});
            skPoint(sketch, "E46.0.2.11", {"position": v(1.71, -19.03) * mm});
            skCircle(sketch, "E46.0.2.12", {"center": v(3.18, -16.5) * mm, "radius": 2.92 * mm, "construction": true});
            skLineSegment(sketch, "E46.0.2.13", {"start": v(18.8, -18.18) * mm, "end": v(15.87, -19.87) * mm});
            skLineSegment(sketch, "E46.0.2.14", {"start": v(15.88, -19.87) * mm, "end": v(12.95, -18.18) * mm});
            skLineSegment(sketch, "E46.0.2.15", {"start": v(-12.45, -18.18) * mm, "end": v(-12.45, -14.81) * mm});
            skLineSegment(sketch, "E46.0.2.16", {"start": v(-0.25, -14.81) * mm, "end": v(-0.25, -18.18) * mm});
            skLineSegment(sketch, "E46.0.2.17", {"start": v(-12.7, -18.62) * mm, "end": v(-9.78, -20.31) * mm});
            skLineSegment(sketch, "E46.0.2.18", {"start": v(-15.62, -23.68) * mm, "end": v(-15.62, -20.31) * mm});
            skLineSegment(sketch, "E46.0.2.19", {"start": v(-19.3, -18.18) * mm, "end": v(-22.23, -19.87) * mm});
            skLineSegment(sketch, "E46.0.2.20", {"start": v(0.25, -18.18) * mm, "end": v(0.25, -14.81) * mm});
            skLineSegment(sketch, "E46.0.2.21", {"start": v(-9.78, -20.31) * mm, "end": v(-9.78, -23.68) * mm});
            skLineSegment(sketch, "E46.0.2.22", {"start": v(15.62, -20.31) * mm, "end": v(15.62, -23.68) * mm});
            skLineSegment(sketch, "E46.0.2.23", {"start": v(-9.78, -23.68) * mm, "end": v(-12.7, -25.37) * mm});
            skLineSegment(sketch, "E46.0.2.24", {"start": v(-22.23, -19.87) * mm, "end": v(-25.15, -18.18) * mm});
            skLineSegment(sketch, "E46.0.2.25", {"start": v(-21.97, -23.68) * mm, "end": v(3.43, -23.68) * mm, "construction": true});
            skLineSegment(sketch, "E46.0.2.26", {"start": v(-12.7, -25.37) * mm, "end": v(-15.62, -23.68) * mm});
            skLineSegment(sketch, "E46.0.2.27", {"start": v(19.05, -18.62) * mm, "end": v(21.97, -20.31) * mm});
            skLineSegment(sketch, "E46.0.2.28", {"start": v(0.25, -18.18) * mm, "end": v(-6.1, -18.18) * mm, "construction": true});
            skLineSegment(sketch, "E46.0.2.29", {"start": v(-21.97, -23.68) * mm, "end": v(-21.97, -12.68) * mm, "construction": true});
            skLineSegment(sketch, "E46.0.2.30", {"start": v(-2.92, -23.68) * mm, "end": v(-9.27, -23.68) * mm, "construction": true});
            skLineSegment(sketch, "E46.0.2.31", {"start": v(25.15, -14.81) * mm, "end": v(25.15, -18.18) * mm});
            skLineSegment(sketch, "E46.0.2.32", {"start": v(16.13, -20.31) * mm, "end": v(19.05, -18.62) * mm});
            skLineSegment(sketch, "E46.0.2.33", {"start": v(-6.6, -18.18) * mm, "end": v(-9.52, -19.87) * mm});
            skLineSegment(sketch, "E46.0.2.34", {"start": v(25.15, -18.18) * mm, "end": v(22.23, -19.87) * mm});
            skLineSegment(sketch, "E46.0.2.35", {"start": v(16.13, -23.68) * mm, "end": v(16.13, -20.31) * mm});
            skLineSegment(sketch, "E46.0.2.36", {"start": v(-6.6, -14.81) * mm, "end": v(-6.6, -18.18) * mm});
            skLineSegment(sketch, "E46.0.2.37", {"start": v(19.05, -25.37) * mm, "end": v(16.13, -23.68) * mm});
            skLineSegment(sketch, "E46.0.2.38", {"start": v(-9.52, -19.87) * mm, "end": v(-12.45, -18.18) * mm});
            skLineSegment(sketch, "E46.0.2.39", {"start": v(-21.97, -20.31) * mm, "end": v(-19.05, -18.62) * mm});
            skLineSegment(sketch, "E46.0.2.40", {"start": v(22.23, -19.87) * mm, "end": v(19.3, -18.18) * mm});
            skLineSegment(sketch, "E46.0.2.41", {"start": v(12.45, -14.81) * mm, "end": v(12.45, -18.18) * mm});
            skLineSegment(sketch, "E46.0.2.42", {"start": v(21.97, -23.68) * mm, "end": v(19.05, -25.37) * mm});
            skLineSegment(sketch, "E46.0.2.43", {"start": v(-18.8, -18.18) * mm, "end": v(-18.8, -14.81) * mm});
            skLineSegment(sketch, "E46.0.2.44", {"start": v(-19.05, -18.62) * mm, "end": v(-16.13, -20.31) * mm});
            skLineSegment(sketch, "E46.0.2.45", {"start": v(19.3, -18.18) * mm, "end": v(19.3, -14.81) * mm});
            skLineSegment(sketch, "E46.0.2.46", {"start": v(12.45, -18.18) * mm, "end": v(9.52, -19.87) * mm});
            skLineSegment(sketch, "E46.0.2.47", {"start": v(21.97, -20.31) * mm, "end": v(21.97, -23.68) * mm});
            skLineSegment(sketch, "E46.0.2.48", {"start": v(-16.13, -20.31) * mm, "end": v(-16.13, -23.68) * mm});
            skLineSegment(sketch, "E46.0.2.49", {"start": v(-9.27, -23.68) * mm, "end": v(-9.27, -20.31) * mm});
            skLineSegment(sketch, "E46.0.2.50", {"start": v(-16.13, -23.68) * mm, "end": v(-19.05, -25.37) * mm});
            skLineSegment(sketch, "E46.0.2.51", {"start": v(-9.27, -20.31) * mm, "end": v(-6.35, -18.62) * mm});
            skLineSegment(sketch, "E46.0.2.52", {"start": v(6.6, -18.18) * mm, "end": v(6.6, -14.81) * mm});
            skLineSegment(sketch, "E46.0.2.53", {"start": v(-12.95, -18.18) * mm, "end": v(-15.88, -19.87) * mm});
            skLineSegment(sketch, "E46.0.2.54", {"start": v(-19.05, -25.37) * mm, "end": v(-21.97, -23.68) * mm});
            skLineSegment(sketch, "E46.0.2.55", {"start": v(-6.35, -18.62) * mm, "end": v(-3.43, -20.31) * mm});
            skLineSegment(sketch, "E46.0.2.56", {"start": v(-12.95, -14.81) * mm, "end": v(-12.95, -18.18) * mm});
            skLineSegment(sketch, "E46.0.2.57", {"start": v(-6.1, -18.18) * mm, "end": v(-6.1, -14.81) * mm});
            skLineSegment(sketch, "E46.0.2.58", {"start": v(-3.43, -20.31) * mm, "end": v(-3.43, -23.68) * mm});
            skLineSegment(sketch, "E46.0.2.59", {"start": v(12.7, -18.62) * mm, "end": v(15.62, -20.31) * mm});
            skLineSegment(sketch, "E46.0.2.60", {"start": v(9.78, -20.31) * mm, "end": v(12.7, -18.62) * mm});
            skLineSegment(sketch, "E46.0.2.61", {"start": v(9.78, -23.68) * mm, "end": v(9.78, -20.31) * mm});
            skCircle(sketch, "E46.0.2.62", {"center": v(0, -22) * mm, "radius": 2.92 * mm, "construction": true});
            skLineSegment(sketch, "E46.0.2.63", {"start": v(6.35, -25.37) * mm, "end": v(3.43, -23.68) * mm});
            skLineSegment(sketch, "E46.0.2.64", {"start": v(9.27, -23.68) * mm, "end": v(6.35, -25.37) * mm});
            skLineSegment(sketch, "E46.0.2.65", {"start": v(9.27, -20.31) * mm, "end": v(9.27, -23.68) * mm});
            skPoint(sketch, "E46.0.2.66", {"position": v(1.71, -19.03) * mm});
            skLineSegment(sketch, "E46.0.2.67", {"start": v(-6.35, -25.37) * mm, "end": v(-9.27, -23.68) * mm});
            skLineSegment(sketch, "E46.0.2.68", {"start": v(0, -22) * mm, "end": v(1.46, -19.47) * mm, "construction": true});
            skLineSegment(sketch, "E46.0.2.69", {"start": v(0.25, -18.18) * mm, "end": v(6.6, -18.18) * mm, "construction": true});
            skLineSegment(sketch, "E46.0.2.70", {"start": v(-2.92, -23.68) * mm, "end": v(3.43, -23.68) * mm, "construction": true});
            skLineSegment(sketch, "E46.0.2.71", {"start": v(6.1, -14.81) * mm, "end": v(6.1, -18.18) * mm});
            skLineSegment(sketch, "E46.0.2.72", {"start": v(6.1, -18.18) * mm, "end": v(3.17, -19.87) * mm});
            skLineSegment(sketch, "E46.0.2.73", {"start": v(-21.97, -23.68) * mm, "end": v(-21.97, -20.31) * mm});
            skLineSegment(sketch, "E46.0.2.74", {"start": v(9.52, -19.87) * mm, "end": v(6.6, -18.18) * mm});
            skLineSegment(sketch, "E46.0.2.75", {"start": v(3.18, -20.31) * mm, "end": v(3.18, -16.5) * mm, "construction": true});
            skLineSegment(sketch, "E46.0.2.76", {"start": v(2.92, -20.31) * mm, "end": v(2.92, -23.68) * mm});
            skLineSegment(sketch, "E46.0.2.77", {"start": v(2.92, -23.68) * mm, "end": v(0, -25.37) * mm});
            skLineSegment(sketch, "E46.0.2.78", {"start": v(0, -25.37) * mm, "end": v(-2.92, -23.68) * mm});
            skLineSegment(sketch, "E46.0.2.79", {"start": v(-2.92, -23.68) * mm, "end": v(-2.92, -20.31) * mm});
            skLineSegment(sketch, "E46.0.2.80", {"start": v(-2.92, -20.31) * mm, "end": v(0, -18.62) * mm});
            skLineSegment(sketch, "E46.0.2.81", {"start": v(6.35, -18.62) * mm, "end": v(9.27, -20.31) * mm});
            skLineSegment(sketch, "E46.0.2.82", {"start": v(3.43, -20.31) * mm, "end": v(6.35, -18.62) * mm});
            skLineSegment(sketch, "E46.0.2.83", {"start": v(3.43, -23.68) * mm, "end": v(3.43, -20.31) * mm});
            skPoint(sketch, "E46.0.2.84", {"position": v(1.71, -19.03) * mm});
            skLineSegment(sketch, "E46.0.2.85", {"start": v(22.23, -13.12) * mm, "end": v(25.15, -14.81) * mm});
            skLineSegment(sketch, "E46.0.2.86", {"start": v(9.52, -13.12) * mm, "end": v(12.45, -14.81) * mm});
            skLineSegment(sketch, "E46.0.2.87", {"start": v(1.46, -19.47) * mm, "end": v(3.18, -16.5) * mm, "construction": true});
            skLineSegment(sketch, "E46.0.2.88", {"start": v(-6.1, -14.81) * mm, "end": v(-3.17, -13.12) * mm});
            skLineSegment(sketch, "E46.0.2.89", {"start": v(-3.17, -13.12) * mm, "end": v(-0.25, -14.81) * mm});
            skLineSegment(sketch, "E46.0.2.90", {"start": v(15.87, -13.12) * mm, "end": v(18.8, -14.81) * mm});
            skLineSegment(sketch, "E46.0.2.91", {"start": v(-22.22, -13.12) * mm, "end": v(-19.3, -14.81) * mm});
            skLineSegment(sketch, "E46.0.2.92", {"start": v(0.25, -14.81) * mm, "end": v(3.18, -13.12) * mm});
            skLineSegment(sketch, "E46.0.2.93", {"start": v(19.3, -14.81) * mm, "end": v(22.23, -13.12) * mm});
            skLineSegment(sketch, "E46.0.2.94", {"start": v(3.18, -13.12) * mm, "end": v(6.1, -14.81) * mm});
            skLineSegment(sketch, "E46.0.2.95", {"start": v(-12.45, -14.81) * mm, "end": v(-9.52, -13.12) * mm});
            skLineSegment(sketch, "E46.0.2.96", {"start": v(-9.52, -13.12) * mm, "end": v(-6.6, -14.81) * mm});
            skLineSegment(sketch, "E46.0.2.97", {"start": v(6.6, -14.81) * mm, "end": v(9.53, -13.12) * mm});
            skLineSegment(sketch, "E46.0.2.98", {"start": v(-18.8, -14.81) * mm, "end": v(-15.88, -13.12) * mm});
            skLineSegment(sketch, "E46.0.2.99", {"start": v(2.92, -20.31) * mm, "end": v(3.43, -20.31) * mm, "construction": true});
            skLineSegment(sketch, "E46.0.2.100", {"start": v(-15.87, -13.12) * mm, "end": v(-12.95, -14.81) * mm});
            skLineSegment(sketch, "E46.0.2.101", {"start": v(12.95, -14.81) * mm, "end": v(15.88, -13.12) * mm});
            skLineSegment(sketch, "E46.0.2.102", {"start": v(0.25, -18.18) * mm, "end": v(3.17, -19.87) * mm, "construction": true});
            skLineSegment(sketch, "E46.0.2.103", {"start": v(0, -18.62) * mm, "end": v(2.92, -20.31) * mm});
            skLineSegment(sketch, "E46.0.2.104", {"start": v(3.18, -19.87) * mm, "end": v(0.25, -18.18) * mm});
            skLineSegment(sketch, "E46.0.2.105", {"start": v(-25.15, -18.18) * mm, "end": v(-25.15, -14.81) * mm});
            skLineSegment(sketch, "E46.0.2.106", {"start": v(-25.15, -14.81) * mm, "end": v(-22.23, -13.12) * mm});
            skLineSegment(sketch, "E46.0.3.0", {"start": v(-0.25, -29.18) * mm, "end": v(-3.17, -30.87) * mm});
            skLineSegment(sketch, "E46.0.3.1", {"start": v(18.8, -25.8) * mm, "end": v(18.8, -29.18) * mm});
            skLineSegment(sketch, "E46.0.3.2", {"start": v(-15.88, -30.87) * mm, "end": v(-18.8, -29.18) * mm});
            skLineSegment(sketch, "E46.0.3.3", {"start": v(-19.3, -25.8) * mm, "end": v(-19.3, -29.18) * mm});
            skLineSegment(sketch, "E46.0.3.4", {"start": v(-3.17, -30.87) * mm, "end": v(-6.1, -29.18) * mm});
            skLineSegment(sketch, "E46.0.3.5", {"start": v(12.95, -29.18) * mm, "end": v(12.95, -25.8) * mm});
            skLineSegment(sketch, "E46.0.3.6", {"start": v(-3.43, -34.68) * mm, "end": v(-6.35, -36.37) * mm});
            skLineSegment(sketch, "E46.0.3.7", {"start": v(-15.62, -31.3) * mm, "end": v(-12.7, -29.62) * mm});
            skLineSegment(sketch, "E46.0.3.8", {"start": v(12.7, -36.37) * mm, "end": v(9.78, -34.68) * mm});
            skLineSegment(sketch, "E46.0.3.9", {"start": v(15.62, -34.68) * mm, "end": v(12.7, -36.37) * mm});
            skPoint(sketch, "E46.0.3.10", {"position": v(2.92, -33) * mm});
            skPoint(sketch, "E46.0.3.11", {"position": v(1.71, -30.03) * mm});
            skCircle(sketch, "E46.0.3.12", {"center": v(3.18, -27.5) * mm, "radius": 2.92 * mm, "construction": true});
            skLineSegment(sketch, "E46.0.3.13", {"start": v(18.8, -29.18) * mm, "end": v(15.87, -30.87) * mm});
            skLineSegment(sketch, "E46.0.3.14", {"start": v(15.88, -30.87) * mm, "end": v(12.95, -29.18) * mm});
            skLineSegment(sketch, "E46.0.3.15", {"start": v(-12.45, -29.18) * mm, "end": v(-12.45, -25.8) * mm});
            skLineSegment(sketch, "E46.0.3.16", {"start": v(-0.25, -25.8) * mm, "end": v(-0.25, -29.18) * mm});
            skLineSegment(sketch, "E46.0.3.17", {"start": v(-12.7, -29.62) * mm, "end": v(-9.78, -31.3) * mm});
            skLineSegment(sketch, "E46.0.3.18", {"start": v(-15.62, -34.68) * mm, "end": v(-15.62, -31.3) * mm});
            skLineSegment(sketch, "E46.0.3.19", {"start": v(-19.3, -29.18) * mm, "end": v(-22.23, -30.87) * mm});
            skLineSegment(sketch, "E46.0.3.20", {"start": v(0.25, -29.18) * mm, "end": v(0.25, -25.8) * mm});
            skLineSegment(sketch, "E46.0.3.21", {"start": v(-9.78, -31.3) * mm, "end": v(-9.78, -34.68) * mm});
            skLineSegment(sketch, "E46.0.3.22", {"start": v(15.62, -31.3) * mm, "end": v(15.62, -34.68) * mm});
            skLineSegment(sketch, "E46.0.3.23", {"start": v(-9.78, -34.68) * mm, "end": v(-12.7, -36.37) * mm});
            skLineSegment(sketch, "E46.0.3.24", {"start": v(-22.23, -30.87) * mm, "end": v(-25.15, -29.18) * mm});
            skLineSegment(sketch, "E46.0.3.25", {"start": v(-21.97, -34.68) * mm, "end": v(3.43, -34.68) * mm, "construction": true});
            skLineSegment(sketch, "E46.0.3.26", {"start": v(-12.7, -36.37) * mm, "end": v(-15.62, -34.68) * mm});
            skLineSegment(sketch, "E46.0.3.27", {"start": v(19.05, -29.62) * mm, "end": v(21.97, -31.3) * mm});
            skLineSegment(sketch, "E46.0.3.28", {"start": v(0.25, -29.18) * mm, "end": v(-6.1, -29.18) * mm, "construction": true});
            skLineSegment(sketch, "E46.0.3.29", {"start": v(-21.97, -34.68) * mm, "end": v(-21.97, -23.68) * mm, "construction": true});
            skLineSegment(sketch, "E46.0.3.30", {"start": v(-2.92, -34.68) * mm, "end": v(-9.27, -34.68) * mm, "construction": true});
            skLineSegment(sketch, "E46.0.3.31", {"start": v(25.15, -25.8) * mm, "end": v(25.15, -29.18) * mm});
            skLineSegment(sketch, "E46.0.3.32", {"start": v(16.13, -31.3) * mm, "end": v(19.05, -29.62) * mm});
            skLineSegment(sketch, "E46.0.3.33", {"start": v(-6.6, -29.18) * mm, "end": v(-9.52, -30.87) * mm});
            skLineSegment(sketch, "E46.0.3.34", {"start": v(25.15, -29.18) * mm, "end": v(22.23, -30.87) * mm});
            skLineSegment(sketch, "E46.0.3.35", {"start": v(16.13, -34.68) * mm, "end": v(16.13, -31.3) * mm});
            skLineSegment(sketch, "E46.0.3.36", {"start": v(-6.6, -25.8) * mm, "end": v(-6.6, -29.18) * mm});
            skLineSegment(sketch, "E46.0.3.37", {"start": v(19.05, -36.37) * mm, "end": v(16.13, -34.68) * mm});
            skLineSegment(sketch, "E46.0.3.38", {"start": v(-9.52, -30.87) * mm, "end": v(-12.45, -29.18) * mm});
            skLineSegment(sketch, "E46.0.3.39", {"start": v(-21.97, -31.3) * mm, "end": v(-19.05, -29.62) * mm});
            skLineSegment(sketch, "E46.0.3.40", {"start": v(22.23, -30.87) * mm, "end": v(19.3, -29.18) * mm});
            skLineSegment(sketch, "E46.0.3.41", {"start": v(12.45, -25.8) * mm, "end": v(12.45, -29.18) * mm});
            skLineSegment(sketch, "E46.0.3.42", {"start": v(21.97, -34.68) * mm, "end": v(19.05, -36.37) * mm});
            skLineSegment(sketch, "E46.0.3.43", {"start": v(-18.8, -29.18) * mm, "end": v(-18.8, -25.8) * mm});
            skLineSegment(sketch, "E46.0.3.44", {"start": v(-19.05, -29.62) * mm, "end": v(-16.13, -31.3) * mm});
            skLineSegment(sketch, "E46.0.3.45", {"start": v(19.3, -29.18) * mm, "end": v(19.3, -25.8) * mm});
            skLineSegment(sketch, "E46.0.3.46", {"start": v(12.45, -29.18) * mm, "end": v(9.52, -30.87) * mm});
            skLineSegment(sketch, "E46.0.3.47", {"start": v(21.97, -31.3) * mm, "end": v(21.97, -34.68) * mm});
            skLineSegment(sketch, "E46.0.3.48", {"start": v(-16.13, -31.3) * mm, "end": v(-16.13, -34.68) * mm});
            skLineSegment(sketch, "E46.0.3.49", {"start": v(-9.27, -34.68) * mm, "end": v(-9.27, -31.3) * mm});
            skLineSegment(sketch, "E46.0.3.50", {"start": v(-16.13, -34.68) * mm, "end": v(-19.05, -36.37) * mm});
            skLineSegment(sketch, "E46.0.3.51", {"start": v(-9.27, -31.3) * mm, "end": v(-6.35, -29.62) * mm});
            skLineSegment(sketch, "E46.0.3.52", {"start": v(6.6, -29.18) * mm, "end": v(6.6, -25.8) * mm});
            skLineSegment(sketch, "E46.0.3.53", {"start": v(-12.95, -29.18) * mm, "end": v(-15.88, -30.87) * mm});
            skLineSegment(sketch, "E46.0.3.54", {"start": v(-19.05, -36.37) * mm, "end": v(-21.97, -34.68) * mm});
            skLineSegment(sketch, "E46.0.3.55", {"start": v(-6.35, -29.62) * mm, "end": v(-3.43, -31.3) * mm});
            skLineSegment(sketch, "E46.0.3.56", {"start": v(-12.95, -25.8) * mm, "end": v(-12.95, -29.18) * mm});
            skLineSegment(sketch, "E46.0.3.57", {"start": v(-6.1, -29.18) * mm, "end": v(-6.1, -25.8) * mm});
            skLineSegment(sketch, "E46.0.3.58", {"start": v(-3.43, -31.3) * mm, "end": v(-3.43, -34.68) * mm});
            skLineSegment(sketch, "E46.0.3.59", {"start": v(12.7, -29.62) * mm, "end": v(15.62, -31.3) * mm});
            skLineSegment(sketch, "E46.0.3.60", {"start": v(9.78, -31.3) * mm, "end": v(12.7, -29.62) * mm});
            skLineSegment(sketch, "E46.0.3.61", {"start": v(9.78, -34.68) * mm, "end": v(9.78, -31.3) * mm});
            skCircle(sketch, "E46.0.3.62", {"center": v(0, -33) * mm, "radius": 2.92 * mm, "construction": true});
            skLineSegment(sketch, "E46.0.3.63", {"start": v(6.35, -36.37) * mm, "end": v(3.43, -34.68) * mm});
            skLineSegment(sketch, "E46.0.3.64", {"start": v(9.27, -34.68) * mm, "end": v(6.35, -36.37) * mm});
            skLineSegment(sketch, "E46.0.3.65", {"start": v(9.27, -31.3) * mm, "end": v(9.27, -34.68) * mm});
            skPoint(sketch, "E46.0.3.66", {"position": v(1.71, -30.03) * mm});
            skLineSegment(sketch, "E46.0.3.67", {"start": v(-6.35, -36.37) * mm, "end": v(-9.27, -34.68) * mm});
            skLineSegment(sketch, "E46.0.3.68", {"start": v(0, -33) * mm, "end": v(1.46, -30.47) * mm, "construction": true});
            skLineSegment(sketch, "E46.0.3.69", {"start": v(0.25, -29.18) * mm, "end": v(6.6, -29.18) * mm, "construction": true});
            skLineSegment(sketch, "E46.0.3.70", {"start": v(-2.92, -34.68) * mm, "end": v(3.43, -34.68) * mm, "construction": true});
            skLineSegment(sketch, "E46.0.3.71", {"start": v(6.1, -25.8) * mm, "end": v(6.1, -29.18) * mm});
            skLineSegment(sketch, "E46.0.3.72", {"start": v(6.1, -29.18) * mm, "end": v(3.17, -30.87) * mm});
            skLineSegment(sketch, "E46.0.3.73", {"start": v(-21.97, -34.68) * mm, "end": v(-21.97, -31.3) * mm});
            skLineSegment(sketch, "E46.0.3.74", {"start": v(9.52, -30.87) * mm, "end": v(6.6, -29.18) * mm});
            skLineSegment(sketch, "E46.0.3.75", {"start": v(3.18, -31.3) * mm, "end": v(3.18, -27.5) * mm, "construction": true});
            skLineSegment(sketch, "E46.0.3.76", {"start": v(2.92, -31.3) * mm, "end": v(2.92, -34.68) * mm});
            skLineSegment(sketch, "E46.0.3.77", {"start": v(2.92, -34.68) * mm, "end": v(0, -36.37) * mm});
            skLineSegment(sketch, "E46.0.3.78", {"start": v(0, -36.37) * mm, "end": v(-2.92, -34.68) * mm});
            skLineSegment(sketch, "E46.0.3.79", {"start": v(-2.92, -34.68) * mm, "end": v(-2.92, -31.3) * mm});
            skLineSegment(sketch, "E46.0.3.80", {"start": v(-2.92, -31.3) * mm, "end": v(0, -29.62) * mm});
            skLineSegment(sketch, "E46.0.3.81", {"start": v(6.35, -29.62) * mm, "end": v(9.27, -31.3) * mm});
            skLineSegment(sketch, "E46.0.3.82", {"start": v(3.43, -31.3) * mm, "end": v(6.35, -29.62) * mm});
            skLineSegment(sketch, "E46.0.3.83", {"start": v(3.43, -34.68) * mm, "end": v(3.43, -31.3) * mm});
            skPoint(sketch, "E46.0.3.84", {"position": v(1.71, -30.03) * mm});
            skLineSegment(sketch, "E46.0.3.85", {"start": v(22.23, -24.12) * mm, "end": v(25.15, -25.8) * mm});
            skLineSegment(sketch, "E46.0.3.86", {"start": v(9.52, -24.12) * mm, "end": v(12.45, -25.8) * mm});
            skLineSegment(sketch, "E46.0.3.87", {"start": v(1.46, -30.47) * mm, "end": v(3.18, -27.5) * mm, "construction": true});
            skLineSegment(sketch, "E46.0.3.88", {"start": v(-6.1, -25.8) * mm, "end": v(-3.17, -24.12) * mm});
            skLineSegment(sketch, "E46.0.3.89", {"start": v(-3.17, -24.12) * mm, "end": v(-0.25, -25.8) * mm});
            skLineSegment(sketch, "E46.0.3.90", {"start": v(15.87, -24.12) * mm, "end": v(18.8, -25.8) * mm});
            skLineSegment(sketch, "E46.0.3.91", {"start": v(-22.22, -24.12) * mm, "end": v(-19.3, -25.8) * mm});
            skLineSegment(sketch, "E46.0.3.92", {"start": v(0.25, -25.8) * mm, "end": v(3.18, -24.12) * mm});
            skLineSegment(sketch, "E46.0.3.93", {"start": v(19.3, -25.8) * mm, "end": v(22.23, -24.12) * mm});
            skLineSegment(sketch, "E46.0.3.94", {"start": v(3.18, -24.12) * mm, "end": v(6.1, -25.8) * mm});
            skLineSegment(sketch, "E46.0.3.95", {"start": v(-12.45, -25.8) * mm, "end": v(-9.52, -24.12) * mm});
            skLineSegment(sketch, "E46.0.3.96", {"start": v(-9.52, -24.12) * mm, "end": v(-6.6, -25.8) * mm});
            skLineSegment(sketch, "E46.0.3.97", {"start": v(6.6, -25.8) * mm, "end": v(9.53, -24.12) * mm});
            skLineSegment(sketch, "E46.0.3.98", {"start": v(-18.8, -25.8) * mm, "end": v(-15.88, -24.12) * mm});
            skLineSegment(sketch, "E46.0.3.99", {"start": v(2.92, -31.3) * mm, "end": v(3.43, -31.3) * mm, "construction": true});
            skLineSegment(sketch, "E46.0.3.100", {"start": v(-15.87, -24.12) * mm, "end": v(-12.95, -25.8) * mm});
            skLineSegment(sketch, "E46.0.3.101", {"start": v(12.95, -25.8) * mm, "end": v(15.88, -24.12) * mm});
            skLineSegment(sketch, "E46.0.3.102", {"start": v(0.25, -29.18) * mm, "end": v(3.17, -30.87) * mm, "construction": true});
            skLineSegment(sketch, "E46.0.3.103", {"start": v(0, -29.62) * mm, "end": v(2.92, -31.3) * mm});
            skLineSegment(sketch, "E46.0.3.104", {"start": v(3.18, -30.87) * mm, "end": v(0.25, -29.18) * mm});
            skLineSegment(sketch, "E46.0.3.105", {"start": v(-25.15, -29.18) * mm, "end": v(-25.15, -25.8) * mm});
            skLineSegment(sketch, "E46.0.3.106", {"start": v(-25.15, -25.8) * mm, "end": v(-22.23, -24.12) * mm});
            skLineSegment(sketch, "E46.direction2", {"start": v(-21.97, -1.69) * mm, "end": v(-21.97, -12.68) * mm, "construction": true});
            skLineSegment(sketch, "E47.0.1.0", {"start": v(-19.3, -36.8) * mm, "end": v(-19.3, -40.18) * mm});
            skLineSegment(sketch, "E47.0.1.1", {"start": v(-22.22, -35.12) * mm, "end": v(-19.3, -36.8) * mm});
            skLineSegment(sketch, "E47.0.1.2", {"start": v(-25.15, -36.8) * mm, "end": v(-22.23, -35.12) * mm});
            skLineSegment(sketch, "E47.0.1.3", {"start": v(-25.15, -40.18) * mm, "end": v(-25.15, -36.8) * mm});
            skLineSegment(sketch, "E47.0.1.4", {"start": v(-22.23, -41.87) * mm, "end": v(-25.15, -40.18) * mm});
            skLineSegment(sketch, "E47.0.1.5", {"start": v(-19.3, -40.18) * mm, "end": v(-22.23, -41.87) * mm});
            skLineSegment(sketch, "E47.0.1.6", {"start": v(-18.8, -36.8) * mm, "end": v(-15.88, -35.12) * mm});
            skLineSegment(sketch, "E47.0.1.7", {"start": v(-18.8, -40.18) * mm, "end": v(-18.8, -36.8) * mm});
            skLineSegment(sketch, "E47.0.1.8", {"start": v(-15.88, -41.87) * mm, "end": v(-18.8, -40.18) * mm});
            skLineSegment(sketch, "E47.0.1.9", {"start": v(-12.95, -40.18) * mm, "end": v(-15.88, -41.87) * mm});
            skLineSegment(sketch, "E47.0.1.10", {"start": v(-12.95, -36.8) * mm, "end": v(-12.95, -40.18) * mm});
            skLineSegment(sketch, "E47.0.1.11", {"start": v(-15.87, -35.12) * mm, "end": v(-12.95, -36.8) * mm});
            skLineSegment(sketch, "E47.0.1.12", {"start": v(-12.45, -36.8) * mm, "end": v(-9.52, -35.12) * mm});
            skLineSegment(sketch, "E47.0.1.13", {"start": v(-9.52, -35.12) * mm, "end": v(-6.6, -36.8) * mm});
            skLineSegment(sketch, "E47.0.1.14", {"start": v(-6.6, -36.8) * mm, "end": v(-6.6, -40.18) * mm});
            skLineSegment(sketch, "E47.0.1.15", {"start": v(-6.6, -40.18) * mm, "end": v(-9.52, -41.87) * mm});
            skLineSegment(sketch, "E47.0.1.16", {"start": v(-9.52, -41.87) * mm, "end": v(-12.45, -40.18) * mm});
            skLineSegment(sketch, "E47.0.1.17", {"start": v(-12.45, -40.18) * mm, "end": v(-12.45, -36.8) * mm});
            skLineSegment(sketch, "E47.0.1.18", {"start": v(-6.1, -40.18) * mm, "end": v(-6.1, -36.8) * mm});
            skLineSegment(sketch, "E47.0.1.19", {"start": v(-6.1, -36.8) * mm, "end": v(-3.17, -35.12) * mm});
            skLineSegment(sketch, "E47.0.1.20", {"start": v(-3.17, -35.12) * mm, "end": v(-0.25, -36.8) * mm});
            skLineSegment(sketch, "E47.0.1.21", {"start": v(-0.25, -36.8) * mm, "end": v(-0.25, -40.18) * mm});
            skLineSegment(sketch, "E47.0.1.22", {"start": v(-0.25, -40.18) * mm, "end": v(-3.17, -41.87) * mm});
            skLineSegment(sketch, "E47.0.1.23", {"start": v(-3.17, -41.87) * mm, "end": v(-6.1, -40.18) * mm});
            skLineSegment(sketch, "E47.0.1.24", {"start": v(0.25, -36.8) * mm, "end": v(3.18, -35.12) * mm});
            skLineSegment(sketch, "E47.0.1.25", {"start": v(0.25, -40.18) * mm, "end": v(0.25, -36.8) * mm});
            skLineSegment(sketch, "E47.0.1.26", {"start": v(6.1, -40.18) * mm, "end": v(3.18, -41.87) * mm});
            skLineSegment(sketch, "E47.0.1.27", {"start": v(6.1, -36.8) * mm, "end": v(6.1, -40.18) * mm});
            skLineSegment(sketch, "E47.0.1.28", {"start": v(3.18, -35.12) * mm, "end": v(6.1, -36.8) * mm});
            skPoint(sketch, "E47.0.1.29", {"position": v(1.71, -41.02) * mm});
            skLineSegment(sketch, "E47.0.1.30", {"start": v(0.25, -40.18) * mm, "end": v(3.17, -41.87) * mm, "construction": true});
            skPoint(sketch, "E47.0.1.31", {"position": v(1.71, -41.02) * mm});
            skLineSegment(sketch, "E47.0.1.32", {"start": v(3.18, -41.87) * mm, "end": v(0.25, -40.18) * mm});
            skPoint(sketch, "E47.0.1.33", {"position": v(1.71, -41.02) * mm});
            skLineSegment(sketch, "E47.0.1.34", {"start": v(6.6, -40.18) * mm, "end": v(6.6, -36.8) * mm});
            skLineSegment(sketch, "E47.0.1.35", {"start": v(6.6, -36.8) * mm, "end": v(9.53, -35.12) * mm});
            skLineSegment(sketch, "E47.0.1.36", {"start": v(9.52, -35.12) * mm, "end": v(12.45, -36.8) * mm});
            skLineSegment(sketch, "E47.0.1.37", {"start": v(12.45, -36.8) * mm, "end": v(12.45, -40.18) * mm});
            skLineSegment(sketch, "E47.0.1.38", {"start": v(12.45, -40.18) * mm, "end": v(9.52, -41.87) * mm});
            skLineSegment(sketch, "E47.0.1.39", {"start": v(9.52, -41.87) * mm, "end": v(6.6, -40.18) * mm});
            skLineSegment(sketch, "E47.0.1.40", {"start": v(12.95, -40.18) * mm, "end": v(12.95, -36.8) * mm});
            skLineSegment(sketch, "E47.0.1.41", {"start": v(12.95, -36.8) * mm, "end": v(15.88, -35.12) * mm});
            skLineSegment(sketch, "E47.0.1.42", {"start": v(15.87, -35.12) * mm, "end": v(18.8, -36.8) * mm});
            skLineSegment(sketch, "E47.0.1.43", {"start": v(18.8, -36.8) * mm, "end": v(18.8, -40.18) * mm});
            skLineSegment(sketch, "E47.0.1.44", {"start": v(18.8, -40.18) * mm, "end": v(15.87, -41.87) * mm});
            skLineSegment(sketch, "E47.0.1.45", {"start": v(15.88, -41.87) * mm, "end": v(12.95, -40.18) * mm});
            skLineSegment(sketch, "E47.0.1.46", {"start": v(19.3, -40.18) * mm, "end": v(19.3, -36.8) * mm});
            skLineSegment(sketch, "E47.0.1.47", {"start": v(19.3, -36.8) * mm, "end": v(22.23, -35.12) * mm});
            skLineSegment(sketch, "E47.0.1.48", {"start": v(22.23, -35.12) * mm, "end": v(25.15, -36.8) * mm});
            skLineSegment(sketch, "E47.0.1.49", {"start": v(25.15, -36.8) * mm, "end": v(25.15, -40.18) * mm});
            skLineSegment(sketch, "E47.0.1.50", {"start": v(25.15, -40.18) * mm, "end": v(22.23, -41.87) * mm});
            skLineSegment(sketch, "E47.0.1.51", {"start": v(22.23, -41.87) * mm, "end": v(19.3, -40.18) * mm});
            skLineSegment(sketch, "E47.direction1", {"start": v(-25.15, -29.18) * mm, "end": v(0.25, -29.18) * mm, "construction": true});
            skLineSegment(sketch, "E47.direction2", {"start": v(-25.15, -29.18) * mm, "end": v(-25.15, -40.18) * mm, "construction": true});
            skSolve(sketch);
        }
        {
            var Q0;
            Q0 = qSketchRegion(id + "F5", true);
            extrude(context, id + "F6", {"entities" : qUnion([Q0]), "operationType" : NewBodyOperationType.REMOVE, "endBound" : BoundingType.UP_TO_NEXT, "oppositeDirection" : true, "depth" : 25.4 * mm, "offsetDistance" : 25.4 * mm});
        }
        {
            var Q0;
            Q0=makeQuery(id+"F1.opExtrude","SWEPT_FACE",FACE,{"disambiguationData":[OSD([sQuery(id+"F0.wireOp",EDGE,"E0.top")])]});
            var sketch = newSketch(context, id + "F7", { "sketchPlane" : qUnion([Q0])});
            skText(sketch, "E48", { "text": "www.innovative3dm.com", "fontName": "OpenSans-Regular.ttf"});
            const initialGuessF7  = {"E48": [-0.02832, 0.04297, 1, 0, 0.00344]};
            skSetInitialGuess(sketch, initialGuessF7);
            skSolve(sketch);
        }
        {
            var Q0;
            Q0 = qSketchRegion(id + "F7", true);
            extrude(context, id + "F8", {"entities" : qUnion([Q0]), "operationType" : NewBodyOperationType.REMOVE, "oppositeDirection" : true, "depth" : 0.5 * mm, "offsetDistance" : 25.4 * mm});
        }
        {
            var Q0;
            Q0=makeQuery(id+"F1.opExtrude","SWEPT_FACE",FACE,{"disambiguationData":[OSD([sQuery(id+"F0.wireOp",EDGE,"E13.bottom")])]});
            var sketch = newSketch(context, id + "F9", { "sketchPlane" : qUnion([Q0])});
            skLineSegment(sketch, "E49", {"start": v(0, 59.02) * mm, "end": v(0, 53.94) * mm, "construction": true});
            skLineSegment(sketch, "E50.0", {"start": v(5.08, 59.02) * mm, "end": v(5.08, 53.94) * mm, "construction": true});
            skArc(sketch, "E51", {"start": v(5.08, 51.26) * mm, "mid": v(7.75, 53.94) * mm, "end": v(5.08, 56.61) * mm});
            skLineSegment(sketch, "E52", {"start": v(5.08, 56.61) * mm, "end": v(0, 56.61) * mm});
            skLineSegment(sketch, "E53", {"start": v(0, 53.94) * mm, "end": v(5.08, 53.94) * mm, "construction": true});
            skLineSegment(sketch, "E54.MirrorCS", {"start": v(5.08, 51.26) * mm, "end": v(0, 51.26) * mm});
            skLineSegment(sketch, "E55.MirrorCS", {"start": v(-5.08, 56.61) * mm, "end": v(0, 56.61) * mm});
            skLineSegment(sketch, "E56.MirrorCS", {"start": v(-5.08, 51.26) * mm, "end": v(0, 51.26) * mm});
            skArc(sketch, "E57.MirrorC", {"start": v(-5.08, 51.26) * mm, "mid": v(-7.75, 53.94) * mm, "end": v(-5.08, 56.61) * mm});
            skSolve(sketch);
        }
        {
            var Q0;
            Q0 = qSketchRegion(id + "F9", true);
            extrude(context, id + "F10", {"entities" : qUnion([Q0]), "operationType" : NewBodyOperationType.REMOVE, "endBound" : BoundingType.UP_TO_NEXT, "oppositeDirection" : true, "depth" : 25.4 * mm, "offsetDistance" : 25.4 * mm});
        }
        {
            var Q0;
            Q0=makeQuery(id+"F1.opExtrude","CAP_EDGE",EDGE,{"disambiguationData":[OSD([sQuery(id+"F0.wireOp",EDGE,"E13.right")])],"isStart":true});
            chamfer(context, id + "F11", {"entities" : qUnion([Q0]), "width" : 7.62 * mm, "tangentPropagation" : true});
        }
        {
            var Q0;
            Q0=makeQuery(id+"F1.opExtrude","CAP_EDGE",EDGE,{"disambiguationData":[OSD([sQuery(id+"F0.wireOp",EDGE,"E13.right")])],"isStart":false});
            chamfer(context, id + "F12", {"entities" : qUnion([Q0]), "width" : 7.62 * mm, "tangentPropagation" : true});
        }
    });
